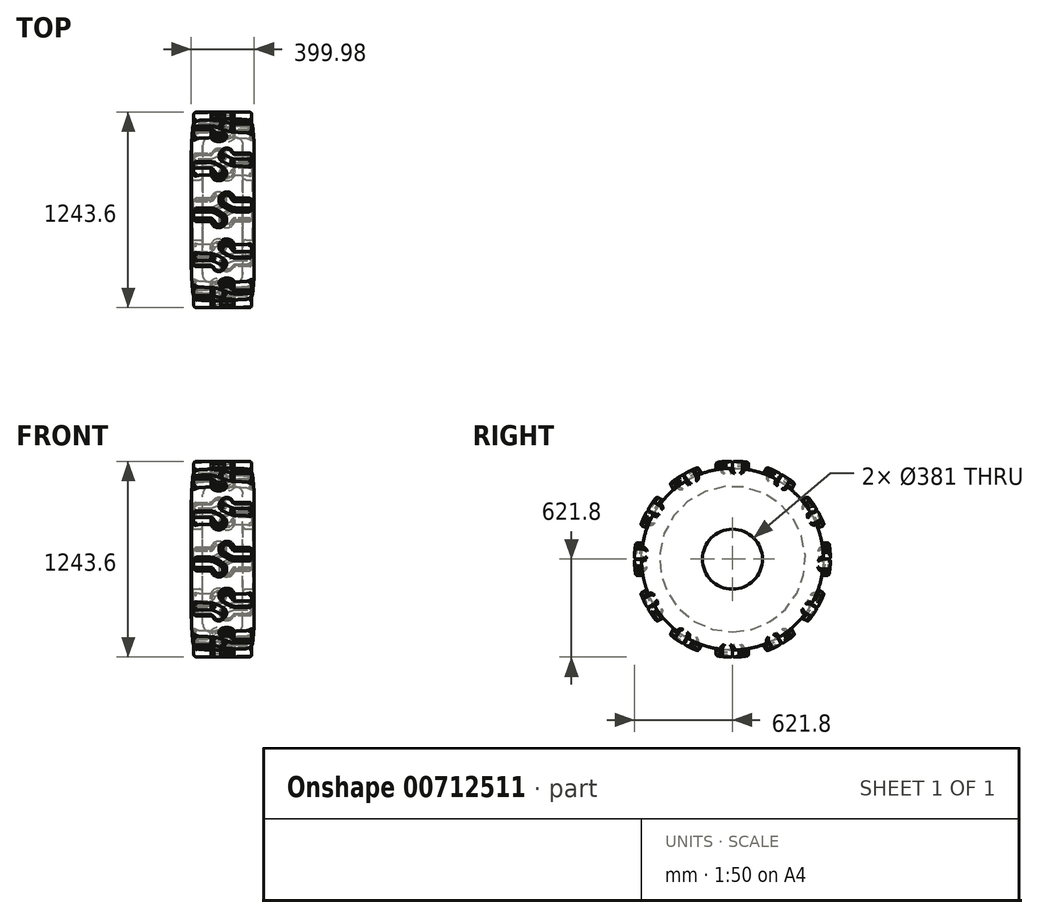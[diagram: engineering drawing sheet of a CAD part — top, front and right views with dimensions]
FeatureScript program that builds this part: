
annotation { "Feature Type Name" : "Feature", "Feature Type Description" : "" }
export const myFeature = defineFeature(function(context is Context, id is Id, definition is map)
    precondition{}
    {
        {
            var Q0;
            Q0=qCreatedBy(makeId("Front.planeOp"),FACE);
            var sketch = newSketch(context, id + "F0", { "sketchPlane" : qUnion([Q0])});
            skLineSegment(sketch, "E0", {"start": v(-266.7, 0) * mm, "end": v(266.7, 0) * mm, "construction": true});
            skLineSegment(sketch, "E1", {"start": v(-190.5, 571.5) * mm, "end": v(190.5, 571.5) * mm, "construction": true});
            skLineSegment(sketch, "E2", {"start": v(0, 0) * mm, "end": v(0, 647.7) * mm, "construction": true});
            skArc(sketch, "E3.trimOffspring", {"start": v(142.07, 574.15) * mm, "mid": v(0, 577.46) * mm, "end": v(-142.07, 574.15) * mm});
            skPoint(sketch, "E4", {"position": v(0, 571.5) * mm});
            skPoint(sketch, "E5.visualSharp", {"position": v(-190.5, 571.5) * mm});
            skArc(sketch, "E5.filletArc", {"start": v(-142.07, 574.15) * mm, "mid": v(-175.89, 559.06) * mm, "end": v(-190.47, 525.02) * mm});
            skPoint(sketch, "E6.visualSharp", {"position": v(190.5, 571.5) * mm});
            skArc(sketch, "E6.filletArc", {"start": v(190.47, 525.02) * mm, "mid": v(175.89, 559.06) * mm, "end": v(142.07, 574.15) * mm});
            skLineSegment(sketch, "E7", {"start": v(-190.5, 0) * mm, "end": v(190.5, 0) * mm});
            skArc(sketch, "E8", {"start": v(-190.74, 521.16) * mm, "mid": v(-194.18, 485.58) * mm, "end": v(-196.78, 449.92) * mm});
            skArc(sketch, "E9", {"start": v(190.5, 190.5) * mm, "mid": v(197.8, 282.59) * mm, "end": v(199.51, 374.95) * mm});
            skLineSegment(sketch, "E10", {"start": v(-190.5, 190.5) * mm, "end": v(190.5, 190.5) * mm});
            skLineSegment(sketch, "E11", {"start": v(-190.5, 190.5) * mm, "end": v(-190.5, 0) * mm});
            skLineSegment(sketch, "E12", {"start": v(190.5, 190.5) * mm, "end": v(190.5, 0) * mm});
            skPoint(sketch, "E13.visualSharp", {"position": v(-190.5, 523.4) * mm});
            skArc(sketch, "E13.filletArc", {"start": v(-190.74, 521.16) * mm, "mid": v(-190.57, 523.09) * mm, "end": v(-190.47, 525.02) * mm});
            skPoint(sketch, "E14.visualSharp", {"position": v(190.5, 523.4) * mm});
            skArc(sketch, "E14.filletArc", {"start": v(190.47, 525.02) * mm, "mid": v(190.57, 523.09) * mm, "end": v(190.74, 521.16) * mm});
            skLineSegment(sketch, "E15", {"start": v(190.5, 0) * mm, "end": v(190.5, 571.5) * mm, "construction": true});
            skLineSegment(sketch, "E16", {"start": v(-190.5, 571.5) * mm, "end": v(-190.5, 0) * mm, "construction": true});
            skArc(sketch, "E17", {"start": v(-197.04, 448.94) * mm, "mid": v(-197.44, 447.47) * mm, "end": v(-197.22, 445.96) * mm});
            skArc(sketch, "E18", {"start": v(-199.66, 378.93) * mm, "mid": v(-199.99, 377.44) * mm, "end": v(-199.7, 375.94) * mm});
            skArc(sketch, "E19.trimOffspring", {"start": v(-199.51, 374.95) * mm, "mid": v(-197.8, 282.59) * mm, "end": v(-190.5, 190.5) * mm});
            skArc(sketch, "E20.trimOffspring", {"start": v(-197.07, 444.95) * mm, "mid": v(-198.6, 412.45) * mm, "end": v(-199.44, 379.92) * mm});
            skPoint(sketch, "E21.visualSharp", {"position": v(-197.04, 445.54) * mm});
            skArc(sketch, "E21.filletArc", {"start": v(-197.07, 444.95) * mm, "mid": v(-197.1, 445.46) * mm, "end": v(-197.22, 445.96) * mm});
            skPoint(sketch, "E22.visualSharp", {"position": v(-196.81, 449.34) * mm});
            skArc(sketch, "E22.filletArc", {"start": v(-197.04, 448.94) * mm, "mid": v(-196.86, 449.42) * mm, "end": v(-196.78, 449.92) * mm});
            skPoint(sketch, "E23.visualSharp", {"position": v(-199.45, 379.34) * mm});
            skArc(sketch, "E23.filletArc", {"start": v(-199.66, 378.93) * mm, "mid": v(-199.5, 379.42) * mm, "end": v(-199.44, 379.92) * mm});
            skPoint(sketch, "E24.visualSharp", {"position": v(-199.5, 375.53) * mm});
            skArc(sketch, "E24.filletArc", {"start": v(-199.51, 374.95) * mm, "mid": v(-199.56, 375.45) * mm, "end": v(-199.7, 375.94) * mm});
            skArc(sketch, "E25.MirrorCS", {"start": v(197.04, 448.94) * mm, "mid": v(197.44, 447.47) * mm, "end": v(197.22, 445.96) * mm});
            skArc(sketch, "E26.MirrorCS", {"start": v(197.04, 448.94) * mm, "mid": v(196.86, 449.42) * mm, "end": v(196.78, 449.92) * mm});
            skArc(sketch, "E27.MirrorCS", {"start": v(197.07, 444.95) * mm, "mid": v(197.1, 445.46) * mm, "end": v(197.22, 445.96) * mm});
            skArc(sketch, "E28.MirrorCS", {"start": v(199.66, 378.93) * mm, "mid": v(199.99, 377.44) * mm, "end": v(199.7, 375.94) * mm});
            skArc(sketch, "E29.MirrorCS", {"start": v(199.66, 378.93) * mm, "mid": v(199.5, 379.42) * mm, "end": v(199.44, 379.92) * mm});
            skArc(sketch, "E30.MirrorCS", {"start": v(199.51, 374.95) * mm, "mid": v(199.56, 375.45) * mm, "end": v(199.7, 375.94) * mm});
            skArc(sketch, "E31.trimOffspring", {"start": v(196.78, 449.92) * mm, "mid": v(194.18, 485.58) * mm, "end": v(190.74, 521.16) * mm});
            skArc(sketch, "E32.trimOffspring", {"start": v(199.44, 379.92) * mm, "mid": v(198.6, 412.45) * mm, "end": v(197.07, 444.95) * mm});
            skSolve(sketch);
        }
        {
            var Q0;
            Q0 = qSketchRegion(id + "F0", true);
            var Q1;
            Q1=sQuery(id+"F0.wireOp",EDGE,"E0");
            revolve(context, id + "F1", {"surfaceOperationType" : NewSurfaceOperationType.NEW, "entities" : qUnion([Q0]), "axis" : qUnion([Q1]), "revolveType" : RevolveType.FULL});
        }
        {
            var Q0;
            Q0=qCreatedBy(makeId("Top.planeOp"),FACE);
            var sketch = newSketch(context, id + "F2", { "sketchPlane" : qUnion([Q0])});
            skLineSegment(sketch, "E33", {"start": v(-184.12, -12.7) * mm, "end": v(-184.12, -50.8) * mm});
            skLineSegment(sketch, "E34", {"start": v(-171.42, -63.5) * mm, "end": v(-82.52, -63.5) * mm});
            skLineSegment(sketch, "E35", {"start": v(-88.6, -52.13) * mm, "end": v(-57.12, -70.3) * mm});
            skLineSegment(sketch, "E36", {"start": v(-6.35, -32.2) * mm, "end": v(-44.42, -10.2) * mm});
            skLineSegment(sketch, "E37", {"start": v(-82.52, 0) * mm, "end": v(-171.42, 0) * mm});
            skLineSegment(sketch, "E38", {"start": v(0, 708.1) * mm, "end": v(0, -708.1) * mm, "construction": true});
            skArc(sketch, "E39", {"start": v(-59.17, -82.83) * mm, "mid": v(0.97, -92.69) * mm, "end": v(-6.35, -32.2) * mm});
            skPoint(sketch, "E40.visualSharp", {"position": v(-62.1, 0) * mm});
            skArc(sketch, "E40.filletArc", {"start": v(-44.42, -10.2) * mm, "mid": v(-62.8, -2.6) * mm, "end": v(-82.52, 0) * mm});
            skArc(sketch, "E41.filletArc", {"start": v(-57.12, -70.3) * mm, "mid": v(-69.38, -65.23) * mm, "end": v(-82.52, -63.5) * mm});
            skPoint(sketch, "E42.visualSharp", {"position": v(-63.47, -66.64) * mm});
            skArc(sketch, "E42.filletArc", {"start": v(-59.17, -82.83) * mm, "mid": v(-71.7, -65.39) * mm, "end": v(-88.6, -52.13) * mm});
            skPoint(sketch, "E43.visualSharp", {"position": v(-184.12, 0) * mm});
            skArc(sketch, "E43.filletArc", {"start": v(-171.42, 0) * mm, "mid": v(-180.4, -3.72) * mm, "end": v(-184.12, -12.7) * mm});
            skPoint(sketch, "E44.visualSharp", {"position": v(-184.12, -63.5) * mm});
            skArc(sketch, "E44.filletArc", {"start": v(-184.12, -50.8) * mm, "mid": v(-180.4, -59.78) * mm, "end": v(-171.42, -63.5) * mm});
            skPoint(sketch, "E45.MirrorP", {"position": v(63.47, -66.64) * mm});
            skLineSegment(sketch, "E46", {"start": v(-306.91, 0) * mm, "end": v(266.7, 0) * mm, "construction": true});
            skSolve(sketch);
        }
        {
            var Q0;
            Q0 = qSketchRegion(id + "F2", true);
            var Q1;
            Q1=sQuery(id+"F0.wireOp",VERTEX,"E2.end");
            extrude(context, id + "F3", {"entities" : qUnion([Q0]), "endBound" : BoundingType.UP_TO_VERTEX, "depth" : 711.2 * mm, "endBoundEntityVertex" : qUnion([Q1]), "offsetDistance" : 25.4 * mm});
        }
        {
            var Q0;
            Q0=makeQuery(id+"F3.opExtrude","SWEPT_BODY",BODY,{"disambiguationData":[OSD([sQuery(id+"F2.wireOp",EDGE,"E33"),sQuery(id+"F2.wireOp",EDGE,"E34"),sQuery(id+"F2.wireOp",EDGE,"E35"),sQuery(id+"F2.wireOp",EDGE,"E36"),sQuery(id+"F2.wireOp",EDGE,"E37"),sQuery(id+"F2.wireOp",EDGE,"E39"),sQuery(id+"F2.wireOp",EDGE,"E40.filletArc"),sQuery(id+"F2.wireOp",EDGE,"E41.filletArc"),sQuery(id+"F2.wireOp",EDGE,"E42.filletArc"),sQuery(id+"F2.wireOp",EDGE,"E43.filletArc"),sQuery(id+"F2.wireOp",EDGE,"E44.filletArc")])]});
            var Q1;
            Q1=qCreatedBy(makeId("Right.planeOp"),FACE);
            mirror(context, id + "F4", {"entities" : qUnion([Q0]), "mirrorPlane" : qUnion([Q1])});
        }
        {
            var Q0;
            Q0=makeQuery(id+"F4.opPattern","COPY",BODY,{"derivedFrom":makeQuery(id+"F3.opExtrude","SWEPT_BODY",BODY,{"disambiguationData":[OSD([sQuery(id+"F2.wireOp",EDGE,"E33"),sQuery(id+"F2.wireOp",EDGE,"E34"),sQuery(id+"F2.wireOp",EDGE,"E35"),sQuery(id+"F2.wireOp",EDGE,"E36"),sQuery(id+"F2.wireOp",EDGE,"E37"),sQuery(id+"F2.wireOp",EDGE,"E39"),sQuery(id+"F2.wireOp",EDGE,"E40.filletArc"),sQuery(id+"F2.wireOp",EDGE,"E41.filletArc"),sQuery(id+"F2.wireOp",EDGE,"E42.filletArc"),sQuery(id+"F2.wireOp",EDGE,"E43.filletArc"),sQuery(id+"F2.wireOp",EDGE,"E44.filletArc")])]}),"instanceName":"1"});
            var Q1;
            Q1=qCreatedBy(makeId("Front.planeOp"),FACE);
            mirror(context, id + "F5", {"entities" : qUnion([Q0]), "mirrorPlane" : qUnion([Q1])});
        }
        {
            var Q0;
            Q0=makeQuery(id+"F4.opPattern","COPY",BODY,{"derivedFrom":makeQuery(id+"F3.opExtrude","SWEPT_BODY",BODY,{"disambiguationData":[OSD([sQuery(id+"F2.wireOp",EDGE,"E33"),sQuery(id+"F2.wireOp",EDGE,"E34"),sQuery(id+"F2.wireOp",EDGE,"E35"),sQuery(id+"F2.wireOp",EDGE,"E36"),sQuery(id+"F2.wireOp",EDGE,"E37"),sQuery(id+"F2.wireOp",EDGE,"E39"),sQuery(id+"F2.wireOp",EDGE,"E40.filletArc"),sQuery(id+"F2.wireOp",EDGE,"E41.filletArc"),sQuery(id+"F2.wireOp",EDGE,"E42.filletArc"),sQuery(id+"F2.wireOp",EDGE,"E43.filletArc"),sQuery(id+"F2.wireOp",EDGE,"E44.filletArc")])]}),"instanceName":"1"});
            deleteBodies(context, id + "F6", {"entities" : qUnion([Q0])});
        }
        {
            var Q0;
            Q0=qCreatedBy(makeId("Front.planeOp"),FACE);
            var sketch = newSketch(context, id + "F7", { "sketchPlane" : qUnion([Q0])});
            skLineSegment(sketch, "E47", {"start": v(-266.7, 0) * mm, "end": v(266.7, 0) * mm, "construction": true});
            skArc(sketch, "E48", {"start": v(266.7, 616.91) * mm, "mid": v(0, 622.3) * mm, "end": v(-266.7, 616.91) * mm});
            skLineSegment(sketch, "E49", {"start": v(266.7, 616.91) * mm, "end": v(266.7, 673.1) * mm});
            skLineSegment(sketch, "E50", {"start": v(266.7, 622.3) * mm, "end": v(-266.7, 622.3) * mm, "construction": true});
            skLineSegment(sketch, "E51", {"start": v(-266.7, 673.1) * mm, "end": v(-266.7, 616.91) * mm});
            skLineSegment(sketch, "E52", {"start": v(0, 0) * mm, "end": v(0, 635) * mm, "construction": true});
            skLineSegment(sketch, "E53", {"start": v(-266.7, 673.1) * mm, "end": v(266.7, 673.1) * mm});
            skSolve(sketch);
        }
        {
            var Q0;
            Q0 = qSketchRegion(id + "F7", true);
            var Q1;
            Q1=sQuery(id+"F7.wireOp",EDGE,"E47");
            revolve(context, id + "F8", {"operationType" : NewBodyOperationType.REMOVE, "surfaceOperationType" : NewSurfaceOperationType.NEW, "entities" : qUnion([Q0]), "axis" : qUnion([Q1]), "revolveType" : RevolveType.FULL, "oppositeDirection" : true});
        }
        {
            var Q0;
            Q0=makeQuery(id+"F3.opExtrude","SWEPT_BODY",BODY,{"disambiguationData":[OSD([sQuery(id+"F2.wireOp",EDGE,"E33"),sQuery(id+"F2.wireOp",EDGE,"E34"),sQuery(id+"F2.wireOp",EDGE,"E35"),sQuery(id+"F2.wireOp",EDGE,"E36"),sQuery(id+"F2.wireOp",EDGE,"E37"),sQuery(id+"F2.wireOp",EDGE,"E39"),sQuery(id+"F2.wireOp",EDGE,"E40.filletArc"),sQuery(id+"F2.wireOp",EDGE,"E41.filletArc"),sQuery(id+"F2.wireOp",EDGE,"E42.filletArc"),sQuery(id+"F2.wireOp",EDGE,"E43.filletArc"),sQuery(id+"F2.wireOp",EDGE,"E44.filletArc")])]});
            var Q1;
            Q1=makeQuery(id+"F5.opPattern","COPY",BODY,{"derivedFrom":makeQuery(id+"F4.opPattern","COPY",BODY,{"derivedFrom":makeQuery(id+"F3.opExtrude","SWEPT_BODY",BODY,{"disambiguationData":[OSD([sQuery(id+"F2.wireOp",EDGE,"E33"),sQuery(id+"F2.wireOp",EDGE,"E34"),sQuery(id+"F2.wireOp",EDGE,"E35"),sQuery(id+"F2.wireOp",EDGE,"E36"),sQuery(id+"F2.wireOp",EDGE,"E37"),sQuery(id+"F2.wireOp",EDGE,"E39"),sQuery(id+"F2.wireOp",EDGE,"E40.filletArc"),sQuery(id+"F2.wireOp",EDGE,"E41.filletArc"),sQuery(id+"F2.wireOp",EDGE,"E42.filletArc"),sQuery(id+"F2.wireOp",EDGE,"E43.filletArc"),sQuery(id+"F2.wireOp",EDGE,"E44.filletArc")])]}),"instanceName":"1"}),"instanceName":"1"});
            var Q2;
            Q2=makeQuery(id+"F1.opRevolve","SWEPT_EDGE",EDGE,{"disambiguationData":[OSD([sQuery(id+"F0.wireOp",EDGE,"E3.trimOffspring"),sQuery(id+"F0.wireOp",EDGE,"E5.filletArc")])]});
            circularPattern(context, id + "F9", {"operationType" : NewBodyOperationType.ADD, "entities" : qUnion([Q0, Q1]), "axis" : qUnion([Q2]), "angle" : 360 * degree, "instanceCount" : 12, "equalSpace" : true, "isCentered" : true});
        }
        {
            var Q0;
            Q0=makeQuery(id+"F8.boolean.opBoolean","INTERSECT",EDGE,{"derivedFrom":[makeQuery(id+"F3.opExtrude","SWEPT_FACE",FACE,{"disambiguationData":[OSD([sQuery(id+"F2.wireOp",EDGE,"E35")])]}),makeQuery(id+"F8.opRevolve","SWEPT_FACE",FACE,{"disambiguationData":[OSD([sQuery(id+"F7.wireOp",EDGE,"E48")])]})]});
            var Q1;
            {var subQ0=makeQuery(id+"F3.opExtrude","SWEPT_FACE",FACE,{"disambiguationData":[OSD([sQuery(id+"F2.wireOp",EDGE,"E33")])]});Q1=makeQuery(id+"F9.boolean.opBoolean","INTERSECT",EDGE,{"disambiguationData":[OD(0.0)],"derivedFrom":[makeQuery(id+"F1.opRevolve","SWEPT_FACE",FACE,{"disambiguationData":[OSD([sQuery(id+"F0.wireOp",EDGE,"E5.filletArc")])]}),subQ0,makeQuery(id+"F9.opPattern","COPY",FACE,{"derivedFrom":subQ0,"instanceName":"-11"}),makeQuery(id+"F9.opPattern","COPY",FACE,{"derivedFrom":subQ0,"instanceName":"-10"}),makeQuery(id+"F9.opPattern","COPY",FACE,{"derivedFrom":subQ0,"instanceName":"-9"}),makeQuery(id+"F9.opPattern","COPY",FACE,{"derivedFrom":subQ0,"instanceName":"-8"}),makeQuery(id+"F9.opPattern","COPY",FACE,{"derivedFrom":subQ0,"instanceName":"-7"}),makeQuery(id+"F9.opPattern","COPY",FACE,{"derivedFrom":subQ0,"instanceName":"-6"}),makeQuery(id+"F9.opPattern","COPY",FACE,{"derivedFrom":subQ0,"instanceName":"-5"}),makeQuery(id+"F9.opPattern","COPY",FACE,{"derivedFrom":subQ0,"instanceName":"-4"}),makeQuery(id+"F9.opPattern","COPY",FACE,{"derivedFrom":subQ0,"instanceName":"-3"}),makeQuery(id+"F9.opPattern","COPY",FACE,{"derivedFrom":subQ0,"instanceName":"-2"}),makeQuery(id+"F9.opPattern","COPY",FACE,{"derivedFrom":subQ0,"instanceName":"-1"}),makeQuery(id+"F9.opPattern","COPY",FACE,{"derivedFrom":subQ0,"instanceName":"1"}),makeQuery(id+"F9.opPattern","COPY",FACE,{"derivedFrom":subQ0,"instanceName":"2"}),makeQuery(id+"F9.opPattern","COPY",FACE,{"derivedFrom":subQ0,"instanceName":"3"}),makeQuery(id+"F9.opPattern","COPY",FACE,{"derivedFrom":subQ0,"instanceName":"4"}),makeQuery(id+"F9.opPattern","COPY",FACE,{"derivedFrom":subQ0,"instanceName":"5"}),makeQuery(id+"F9.opPattern","COPY",FACE,{"derivedFrom":subQ0,"instanceName":"6"}),makeQuery(id+"F9.opPattern","COPY",FACE,{"derivedFrom":subQ0,"instanceName":"7"}),makeQuery(id+"F9.opPattern","COPY",FACE,{"derivedFrom":subQ0,"instanceName":"8"}),makeQuery(id+"F9.opPattern","COPY",FACE,{"derivedFrom":subQ0,"instanceName":"9"}),makeQuery(id+"F9.opPattern","COPY",FACE,{"derivedFrom":subQ0,"instanceName":"10"}),makeQuery(id+"F9.opPattern","COPY",FACE,{"derivedFrom":subQ0,"instanceName":"11"})]});}
            var Q2;
            Q2=makeQuery(id+"F9.boolean.opBoolean","INTERSECT",EDGE,{"derivedFrom":[makeQuery(id+"F1.opRevolve","SWEPT_FACE",FACE,{"disambiguationData":[OSD([sQuery(id+"F0.wireOp",EDGE,"E3.trimOffspring")])]}),makeQuery(id+"F5.opPattern","COPY",FACE,{"derivedFrom":makeQuery(id+"F4.opPattern","COPY",FACE,{"derivedFrom":makeQuery(id+"F3.opExtrude","SWEPT_FACE",FACE,{"disambiguationData":[OSD([sQuery(id+"F2.wireOp",EDGE,"E36")])]}),"instanceName":"1"}),"instanceName":"1"})]});
            var Q3;
            Q3=makeQuery(id+"F8.boolean.opBoolean","INTERSECT",EDGE,{"derivedFrom":[makeQuery(id+"F5.opPattern","COPY",FACE,{"derivedFrom":makeQuery(id+"F4.opPattern","COPY",FACE,{"derivedFrom":makeQuery(id+"F3.opExtrude","SWEPT_FACE",FACE,{"disambiguationData":[OSD([sQuery(id+"F2.wireOp",EDGE,"E36")])]}),"instanceName":"1"}),"instanceName":"1"}),makeQuery(id+"F8.opRevolve","SWEPT_FACE",FACE,{"disambiguationData":[OSD([sQuery(id+"F7.wireOp",EDGE,"E48")])]})]});
            var Q4;
            Q4=makeQuery(id+"F9.opPattern","COPY",EDGE,{"derivedFrom":makeQuery(id+"F8.boolean.opBoolean","INTERSECT",EDGE,{"derivedFrom":[makeQuery(id+"F5.opPattern","COPY",FACE,{"derivedFrom":makeQuery(id+"F4.opPattern","COPY",FACE,{"derivedFrom":makeQuery(id+"F3.opExtrude","SWEPT_FACE",FACE,{"disambiguationData":[OSD([sQuery(id+"F2.wireOp",EDGE,"E39")])]}),"instanceName":"1"}),"instanceName":"1"}),makeQuery(id+"F8.opRevolve","SWEPT_FACE",FACE,{"disambiguationData":[OSD([sQuery(id+"F7.wireOp",EDGE,"E48")])]})]}),"instanceName":"-1"});
            var Q5;
            Q5=makeQuery(id+"F9.boolean.opBoolean","INTERSECT",EDGE,{"derivedFrom":[makeQuery(id+"F1.opRevolve","SWEPT_FACE",FACE,{"disambiguationData":[OSD([sQuery(id+"F0.wireOp",EDGE,"E3.trimOffspring")])]}),makeQuery(id+"F9.opPattern","COPY",FACE,{"derivedFrom":makeQuery(id+"F5.opPattern","COPY",FACE,{"derivedFrom":makeQuery(id+"F4.opPattern","COPY",FACE,{"derivedFrom":makeQuery(id+"F3.opExtrude","SWEPT_FACE",FACE,{"disambiguationData":[OSD([sQuery(id+"F2.wireOp",EDGE,"E39")])]}),"instanceName":"1"}),"instanceName":"1"}),"instanceName":"-1"})]});
            var Q6;
            Q6=makeQuery(id+"F9.opPattern","COPY",EDGE,{"derivedFrom":makeQuery(id+"F8.boolean.opBoolean","INTERSECT",EDGE,{"derivedFrom":[makeQuery(id+"F3.opExtrude","SWEPT_FACE",FACE,{"disambiguationData":[OSD([sQuery(id+"F2.wireOp",EDGE,"E37")])]}),makeQuery(id+"F8.opRevolve","SWEPT_FACE",FACE,{"disambiguationData":[OSD([sQuery(id+"F7.wireOp",EDGE,"E48")])]})]}),"instanceName":"-1"});
            var Q7;
            Q7=makeQuery(id+"F9.boolean.opBoolean","INTERSECT",EDGE,{"derivedFrom":[makeQuery(id+"F1.opRevolve","SWEPT_FACE",FACE,{"disambiguationData":[OSD([sQuery(id+"F0.wireOp",EDGE,"E3.trimOffspring")])]}),makeQuery(id+"F9.opPattern","COPY",FACE,{"derivedFrom":makeQuery(id+"F3.opExtrude","SWEPT_FACE",FACE,{"disambiguationData":[OSD([sQuery(id+"F2.wireOp",EDGE,"E37")])]}),"instanceName":"-1"})]});
            var Q8;
            Q8=makeQuery(id+"F9.opPattern","COPY",EDGE,{"derivedFrom":makeQuery(id+"F8.boolean.opBoolean","INTERSECT",EDGE,{"derivedFrom":[makeQuery(id+"F3.opExtrude","SWEPT_FACE",FACE,{"disambiguationData":[OSD([sQuery(id+"F2.wireOp",EDGE,"E39")])]}),makeQuery(id+"F8.opRevolve","SWEPT_FACE",FACE,{"disambiguationData":[OSD([sQuery(id+"F7.wireOp",EDGE,"E48")])]})]}),"instanceName":"-2"});
            var Q9;
            Q9=makeQuery(id+"F9.opPattern","COPY",EDGE,{"derivedFrom":makeQuery(id+"F8.boolean.opBoolean","INTERSECT",EDGE,{"derivedFrom":[makeQuery(id+"F5.opPattern","COPY",FACE,{"derivedFrom":makeQuery(id+"F4.opPattern","COPY",FACE,{"derivedFrom":makeQuery(id+"F3.opExtrude","SWEPT_FACE",FACE,{"disambiguationData":[OSD([sQuery(id+"F2.wireOp",EDGE,"E36")])]}),"instanceName":"1"}),"instanceName":"1"}),makeQuery(id+"F8.opRevolve","SWEPT_FACE",FACE,{"disambiguationData":[OSD([sQuery(id+"F7.wireOp",EDGE,"E48")])]})]}),"instanceName":"-2"});
            var Q10;
            Q10=makeQuery(id+"F9.boolean.opBoolean","INTERSECT",EDGE,{"derivedFrom":[makeQuery(id+"F1.opRevolve","SWEPT_FACE",FACE,{"disambiguationData":[OSD([sQuery(id+"F0.wireOp",EDGE,"E3.trimOffspring")])]}),makeQuery(id+"F9.opPattern","COPY",FACE,{"derivedFrom":makeQuery(id+"F5.opPattern","COPY",FACE,{"derivedFrom":makeQuery(id+"F4.opPattern","COPY",FACE,{"derivedFrom":makeQuery(id+"F3.opExtrude","SWEPT_FACE",FACE,{"disambiguationData":[OSD([sQuery(id+"F2.wireOp",EDGE,"E36")])]}),"instanceName":"1"}),"instanceName":"1"}),"instanceName":"-2"})]});
            var Q11;
            Q11=makeQuery(id+"F9.boolean.opBoolean","INTERSECT",EDGE,{"derivedFrom":[makeQuery(id+"F1.opRevolve","SWEPT_FACE",FACE,{"disambiguationData":[OSD([sQuery(id+"F0.wireOp",EDGE,"E3.trimOffspring")])]}),makeQuery(id+"F9.opPattern","COPY",FACE,{"derivedFrom":makeQuery(id+"F3.opExtrude","SWEPT_FACE",FACE,{"disambiguationData":[OSD([sQuery(id+"F2.wireOp",EDGE,"E39")])]}),"instanceName":"-2"})]});
            var Q12;
            Q12=makeQuery(id+"F9.opPattern","COPY",EDGE,{"derivedFrom":makeQuery(id+"F8.boolean.opBoolean","INTERSECT",EDGE,{"derivedFrom":[makeQuery(id+"F3.opExtrude","SWEPT_FACE",FACE,{"disambiguationData":[OSD([sQuery(id+"F2.wireOp",EDGE,"E39")])]}),makeQuery(id+"F8.opRevolve","SWEPT_FACE",FACE,{"disambiguationData":[OSD([sQuery(id+"F7.wireOp",EDGE,"E48")])]})]}),"instanceName":"-3"});
            var Q13;
            Q13=makeQuery(id+"F9.opPattern","COPY",EDGE,{"derivedFrom":makeQuery(id+"F8.boolean.opBoolean","INTERSECT",EDGE,{"derivedFrom":[makeQuery(id+"F5.opPattern","COPY",FACE,{"derivedFrom":makeQuery(id+"F4.opPattern","COPY",FACE,{"derivedFrom":makeQuery(id+"F3.opExtrude","SWEPT_FACE",FACE,{"disambiguationData":[OSD([sQuery(id+"F2.wireOp",EDGE,"E36")])]}),"instanceName":"1"}),"instanceName":"1"}),makeQuery(id+"F8.opRevolve","SWEPT_FACE",FACE,{"disambiguationData":[OSD([sQuery(id+"F7.wireOp",EDGE,"E48")])]})]}),"instanceName":"-4"});
            var Q14;
            Q14=makeQuery(id+"F9.boolean.opBoolean","INTERSECT",EDGE,{"derivedFrom":[makeQuery(id+"F1.opRevolve","SWEPT_FACE",FACE,{"disambiguationData":[OSD([sQuery(id+"F0.wireOp",EDGE,"E3.trimOffspring")])]}),makeQuery(id+"F9.opPattern","COPY",FACE,{"derivedFrom":makeQuery(id+"F3.opExtrude","SWEPT_FACE",FACE,{"disambiguationData":[OSD([sQuery(id+"F2.wireOp",EDGE,"E39")])]}),"instanceName":"-3"})]});
            var Q15;
            Q15=makeQuery(id+"F9.boolean.opBoolean","INTERSECT",EDGE,{"derivedFrom":[makeQuery(id+"F1.opRevolve","SWEPT_FACE",FACE,{"disambiguationData":[OSD([sQuery(id+"F0.wireOp",EDGE,"E3.trimOffspring")])]}),makeQuery(id+"F9.opPattern","COPY",FACE,{"derivedFrom":makeQuery(id+"F5.opPattern","COPY",FACE,{"derivedFrom":makeQuery(id+"F4.opPattern","COPY",FACE,{"derivedFrom":makeQuery(id+"F3.opExtrude","SWEPT_FACE",FACE,{"disambiguationData":[OSD([sQuery(id+"F2.wireOp",EDGE,"E40.filletArc")])]}),"instanceName":"1"}),"instanceName":"1"}),"instanceName":"-4"})]});
            var Q16;
            Q16=makeQuery(id+"F9.opPattern","COPY",EDGE,{"derivedFrom":makeQuery(id+"F8.boolean.opBoolean","INTERSECT",EDGE,{"derivedFrom":[makeQuery(id+"F3.opExtrude","SWEPT_FACE",FACE,{"disambiguationData":[OSD([sQuery(id+"F2.wireOp",EDGE,"E39")])]}),makeQuery(id+"F8.opRevolve","SWEPT_FACE",FACE,{"disambiguationData":[OSD([sQuery(id+"F7.wireOp",EDGE,"E48")])]})]}),"instanceName":"-4"});
            var Q17;
            Q17=makeQuery(id+"F9.boolean.opBoolean","INTERSECT",EDGE,{"derivedFrom":[makeQuery(id+"F1.opRevolve","SWEPT_FACE",FACE,{"disambiguationData":[OSD([sQuery(id+"F0.wireOp",EDGE,"E3.trimOffspring")])]}),makeQuery(id+"F9.opPattern","COPY",FACE,{"derivedFrom":makeQuery(id+"F3.opExtrude","SWEPT_FACE",FACE,{"disambiguationData":[OSD([sQuery(id+"F2.wireOp",EDGE,"E39")])]}),"instanceName":"-4"})]});
            var Q18;
            Q18=makeQuery(id+"F9.opPattern","COPY",EDGE,{"derivedFrom":makeQuery(id+"F8.boolean.opBoolean","INTERSECT",EDGE,{"derivedFrom":[makeQuery(id+"F3.opExtrude","SWEPT_FACE",FACE,{"disambiguationData":[OSD([sQuery(id+"F2.wireOp",EDGE,"E39")])]}),makeQuery(id+"F8.opRevolve","SWEPT_FACE",FACE,{"disambiguationData":[OSD([sQuery(id+"F7.wireOp",EDGE,"E48")])]})]}),"instanceName":"-8"});
            var Q19;
            Q19=makeQuery(id+"F9.boolean.opBoolean","INTERSECT",EDGE,{"derivedFrom":[makeQuery(id+"F1.opRevolve","SWEPT_FACE",FACE,{"disambiguationData":[OSD([sQuery(id+"F0.wireOp",EDGE,"E3.trimOffspring")])]}),makeQuery(id+"F9.opPattern","COPY",FACE,{"derivedFrom":makeQuery(id+"F3.opExtrude","SWEPT_FACE",FACE,{"disambiguationData":[OSD([sQuery(id+"F2.wireOp",EDGE,"E39")])]}),"instanceName":"-8"})]});
            var Q20;
            Q20=makeQuery(id+"F9.opPattern","COPY",EDGE,{"derivedFrom":makeQuery(id+"F8.boolean.opBoolean","INTERSECT",EDGE,{"derivedFrom":[makeQuery(id+"F5.opPattern","COPY",FACE,{"derivedFrom":makeQuery(id+"F4.opPattern","COPY",FACE,{"derivedFrom":makeQuery(id+"F3.opExtrude","SWEPT_FACE",FACE,{"disambiguationData":[OSD([sQuery(id+"F2.wireOp",EDGE,"E36")])]}),"instanceName":"1"}),"instanceName":"1"}),makeQuery(id+"F8.opRevolve","SWEPT_FACE",FACE,{"disambiguationData":[OSD([sQuery(id+"F7.wireOp",EDGE,"E48")])]})]}),"instanceName":"-8"});
            var Q21;
            Q21=makeQuery(id+"F9.boolean.opBoolean","INTERSECT",EDGE,{"derivedFrom":[makeQuery(id+"F1.opRevolve","SWEPT_FACE",FACE,{"disambiguationData":[OSD([sQuery(id+"F0.wireOp",EDGE,"E3.trimOffspring")])]}),makeQuery(id+"F9.opPattern","COPY",FACE,{"derivedFrom":makeQuery(id+"F5.opPattern","COPY",FACE,{"derivedFrom":makeQuery(id+"F4.opPattern","COPY",FACE,{"derivedFrom":makeQuery(id+"F3.opExtrude","SWEPT_FACE",FACE,{"disambiguationData":[OSD([sQuery(id+"F2.wireOp",EDGE,"E36")])]}),"instanceName":"1"}),"instanceName":"1"}),"instanceName":"-8"})]});
            var Q22;
            Q22=makeQuery(id+"F9.opPattern","COPY",EDGE,{"derivedFrom":makeQuery(id+"F8.boolean.opBoolean","INTERSECT",EDGE,{"derivedFrom":[makeQuery(id+"F5.opPattern","COPY",FACE,{"derivedFrom":makeQuery(id+"F4.opPattern","COPY",FACE,{"derivedFrom":makeQuery(id+"F3.opExtrude","SWEPT_FACE",FACE,{"disambiguationData":[OSD([sQuery(id+"F2.wireOp",EDGE,"E39")])]}),"instanceName":"1"}),"instanceName":"1"}),makeQuery(id+"F8.opRevolve","SWEPT_FACE",FACE,{"disambiguationData":[OSD([sQuery(id+"F7.wireOp",EDGE,"E48")])]})]}),"instanceName":"-9"});
            var Q23;
            Q23=makeQuery(id+"F9.boolean.opBoolean","INTERSECT",EDGE,{"derivedFrom":[makeQuery(id+"F1.opRevolve","SWEPT_FACE",FACE,{"disambiguationData":[OSD([sQuery(id+"F0.wireOp",EDGE,"E3.trimOffspring")])]}),makeQuery(id+"F9.opPattern","COPY",FACE,{"derivedFrom":makeQuery(id+"F5.opPattern","COPY",FACE,{"derivedFrom":makeQuery(id+"F4.opPattern","COPY",FACE,{"derivedFrom":makeQuery(id+"F3.opExtrude","SWEPT_FACE",FACE,{"disambiguationData":[OSD([sQuery(id+"F2.wireOp",EDGE,"E36")])]}),"instanceName":"1"}),"instanceName":"1"}),"instanceName":"-9"})]});
            var Q24;
            Q24=makeQuery(id+"F9.opPattern","COPY",EDGE,{"derivedFrom":makeQuery(id+"F8.boolean.opBoolean","INTERSECT",EDGE,{"derivedFrom":[makeQuery(id+"F3.opExtrude","SWEPT_FACE",FACE,{"disambiguationData":[OSD([sQuery(id+"F2.wireOp",EDGE,"E36")])]}),makeQuery(id+"F8.opRevolve","SWEPT_FACE",FACE,{"disambiguationData":[OSD([sQuery(id+"F7.wireOp",EDGE,"E48")])]})]}),"instanceName":"-9"});
            var Q25;
            Q25=makeQuery(id+"F9.boolean.opBoolean","INTERSECT",EDGE,{"derivedFrom":[makeQuery(id+"F1.opRevolve","SWEPT_FACE",FACE,{"disambiguationData":[OSD([sQuery(id+"F0.wireOp",EDGE,"E3.trimOffspring")])]}),makeQuery(id+"F9.opPattern","COPY",FACE,{"derivedFrom":makeQuery(id+"F3.opExtrude","SWEPT_FACE",FACE,{"disambiguationData":[OSD([sQuery(id+"F2.wireOp",EDGE,"E42.filletArc")])]}),"instanceName":"-9"})]});
            var Q26;
            Q26=makeQuery(id+"F9.opPattern","COPY",EDGE,{"derivedFrom":makeQuery(id+"F8.boolean.opBoolean","INTERSECT",EDGE,{"derivedFrom":[makeQuery(id+"F5.opPattern","COPY",FACE,{"derivedFrom":makeQuery(id+"F4.opPattern","COPY",FACE,{"derivedFrom":makeQuery(id+"F3.opExtrude","SWEPT_FACE",FACE,{"disambiguationData":[OSD([sQuery(id+"F2.wireOp",EDGE,"E37")])]}),"instanceName":"1"}),"instanceName":"1"}),makeQuery(id+"F8.opRevolve","SWEPT_FACE",FACE,{"disambiguationData":[OSD([sQuery(id+"F7.wireOp",EDGE,"E48")])]})]}),"instanceName":"-10"});
            var Q27;
            Q27=makeQuery(id+"F9.opPattern","COPY",EDGE,{"derivedFrom":makeQuery(id+"F8.boolean.opBoolean","INTERSECT",EDGE,{"derivedFrom":[makeQuery(id+"F3.opExtrude","SWEPT_FACE",FACE,{"disambiguationData":[OSD([sQuery(id+"F2.wireOp",EDGE,"E39")])]}),makeQuery(id+"F8.opRevolve","SWEPT_FACE",FACE,{"disambiguationData":[OSD([sQuery(id+"F7.wireOp",EDGE,"E48")])]})]}),"instanceName":"-10"});
            var Q28;
            Q28=makeQuery(id+"F9.boolean.opBoolean","INTERSECT",EDGE,{"derivedFrom":[makeQuery(id+"F1.opRevolve","SWEPT_FACE",FACE,{"disambiguationData":[OSD([sQuery(id+"F0.wireOp",EDGE,"E3.trimOffspring")])]}),makeQuery(id+"F9.opPattern","COPY",FACE,{"derivedFrom":makeQuery(id+"F3.opExtrude","SWEPT_FACE",FACE,{"disambiguationData":[OSD([sQuery(id+"F2.wireOp",EDGE,"E39")])]}),"instanceName":"-10"})]});
            var Q29;
            Q29=makeQuery(id+"F9.boolean.opBoolean","INTERSECT",EDGE,{"derivedFrom":[makeQuery(id+"F1.opRevolve","SWEPT_FACE",FACE,{"disambiguationData":[OSD([sQuery(id+"F0.wireOp",EDGE,"E3.trimOffspring")])]}),makeQuery(id+"F9.opPattern","COPY",FACE,{"derivedFrom":makeQuery(id+"F5.opPattern","COPY",FACE,{"derivedFrom":makeQuery(id+"F4.opPattern","COPY",FACE,{"derivedFrom":makeQuery(id+"F3.opExtrude","SWEPT_FACE",FACE,{"disambiguationData":[OSD([sQuery(id+"F2.wireOp",EDGE,"E37")])]}),"instanceName":"1"}),"instanceName":"1"}),"instanceName":"-10"})]});
            var Q30;
            Q30=makeQuery(id+"F9.opPattern","COPY",EDGE,{"derivedFrom":makeQuery(id+"F8.boolean.opBoolean","INTERSECT",EDGE,{"derivedFrom":[makeQuery(id+"F5.opPattern","COPY",FACE,{"derivedFrom":makeQuery(id+"F4.opPattern","COPY",FACE,{"derivedFrom":makeQuery(id+"F3.opExtrude","SWEPT_FACE",FACE,{"disambiguationData":[OSD([sQuery(id+"F2.wireOp",EDGE,"E37")])]}),"instanceName":"1"}),"instanceName":"1"}),makeQuery(id+"F8.opRevolve","SWEPT_FACE",FACE,{"disambiguationData":[OSD([sQuery(id+"F7.wireOp",EDGE,"E48")])]})]}),"instanceName":"-11"});
            var Q31;
            Q31=makeQuery(id+"F9.boolean.opBoolean","INTERSECT",EDGE,{"derivedFrom":[makeQuery(id+"F1.opRevolve","SWEPT_FACE",FACE,{"disambiguationData":[OSD([sQuery(id+"F0.wireOp",EDGE,"E6.filletArc")])]}),makeQuery(id+"F9.opPattern","COPY",FACE,{"derivedFrom":makeQuery(id+"F5.opPattern","COPY",FACE,{"derivedFrom":makeQuery(id+"F4.opPattern","COPY",FACE,{"derivedFrom":makeQuery(id+"F3.opExtrude","SWEPT_FACE",FACE,{"disambiguationData":[OSD([sQuery(id+"F2.wireOp",EDGE,"E43.filletArc")])]}),"instanceName":"1"}),"instanceName":"1"}),"instanceName":"-11"})]});
            var Q32;
            Q32=makeQuery(id+"F9.opPattern","COPY",EDGE,{"derivedFrom":makeQuery(id+"F8.boolean.opBoolean","INTERSECT",EDGE,{"derivedFrom":[makeQuery(id+"F3.opExtrude","SWEPT_FACE",FACE,{"disambiguationData":[OSD([sQuery(id+"F2.wireOp",EDGE,"E39")])]}),makeQuery(id+"F8.opRevolve","SWEPT_FACE",FACE,{"disambiguationData":[OSD([sQuery(id+"F7.wireOp",EDGE,"E48")])]})]}),"instanceName":"-11"});
            var Q33;
            Q33=makeQuery(id+"F9.boolean.opBoolean","INTERSECT",EDGE,{"derivedFrom":[makeQuery(id+"F1.opRevolve","SWEPT_FACE",FACE,{"disambiguationData":[OSD([sQuery(id+"F0.wireOp",EDGE,"E3.trimOffspring")])]}),makeQuery(id+"F9.opPattern","COPY",FACE,{"derivedFrom":makeQuery(id+"F3.opExtrude","SWEPT_FACE",FACE,{"disambiguationData":[OSD([sQuery(id+"F2.wireOp",EDGE,"E39")])]}),"instanceName":"-11"})]});
            var Q34;
            Q34=makeQuery(id+"F9.opPattern","COPY",EDGE,{"derivedFrom":makeQuery(id+"F8.boolean.opBoolean","INTERSECT",EDGE,{"derivedFrom":[makeQuery(id+"F3.opExtrude","SWEPT_FACE",FACE,{"disambiguationData":[OSD([sQuery(id+"F2.wireOp",EDGE,"E39")])]}),makeQuery(id+"F8.opRevolve","SWEPT_FACE",FACE,{"disambiguationData":[OSD([sQuery(id+"F7.wireOp",EDGE,"E48")])]})]}),"instanceName":"-5"});
            var Q35;
            Q35=makeQuery(id+"F9.opPattern","COPY",EDGE,{"derivedFrom":makeQuery(id+"F8.boolean.opBoolean","INTERSECT",EDGE,{"derivedFrom":[makeQuery(id+"F5.opPattern","COPY",FACE,{"derivedFrom":makeQuery(id+"F4.opPattern","COPY",FACE,{"derivedFrom":makeQuery(id+"F3.opExtrude","SWEPT_FACE",FACE,{"disambiguationData":[OSD([sQuery(id+"F2.wireOp",EDGE,"E33")])]}),"instanceName":"1"}),"instanceName":"1"}),makeQuery(id+"F8.opRevolve","SWEPT_FACE",FACE,{"disambiguationData":[OSD([sQuery(id+"F7.wireOp",EDGE,"E48")])]})]}),"instanceName":"-5"});
            var Q36;
            Q36=makeQuery(id+"F9.boolean.opBoolean","INTERSECT",EDGE,{"derivedFrom":[makeQuery(id+"F1.opRevolve","SWEPT_FACE",FACE,{"disambiguationData":[OSD([sQuery(id+"F0.wireOp",EDGE,"E3.trimOffspring")])]}),makeQuery(id+"F9.opPattern","COPY",FACE,{"derivedFrom":makeQuery(id+"F5.opPattern","COPY",FACE,{"derivedFrom":makeQuery(id+"F4.opPattern","COPY",FACE,{"derivedFrom":makeQuery(id+"F3.opExtrude","SWEPT_FACE",FACE,{"disambiguationData":[OSD([sQuery(id+"F2.wireOp",EDGE,"E34")])]}),"instanceName":"1"}),"instanceName":"1"}),"instanceName":"-5"})]});
            var Q37;
            Q37=makeQuery(id+"F9.boolean.opBoolean","INTERSECT",EDGE,{"derivedFrom":[makeQuery(id+"F1.opRevolve","SWEPT_FACE",FACE,{"disambiguationData":[OSD([sQuery(id+"F0.wireOp",EDGE,"E3.trimOffspring")])]}),makeQuery(id+"F9.opPattern","COPY",FACE,{"derivedFrom":makeQuery(id+"F3.opExtrude","SWEPT_FACE",FACE,{"disambiguationData":[OSD([sQuery(id+"F2.wireOp",EDGE,"E37")])]}),"instanceName":"-5"})]});
            var Q38;
            Q38=makeQuery(id+"F9.boolean.opBoolean","INTERSECT",EDGE,{"derivedFrom":[makeQuery(id+"F1.opRevolve","SWEPT_FACE",FACE,{"disambiguationData":[OSD([sQuery(id+"F0.wireOp",EDGE,"E3.trimOffspring")])]}),makeQuery(id+"F9.opPattern","COPY",FACE,{"derivedFrom":makeQuery(id+"F5.opPattern","COPY",FACE,{"derivedFrom":makeQuery(id+"F4.opPattern","COPY",FACE,{"derivedFrom":makeQuery(id+"F3.opExtrude","SWEPT_FACE",FACE,{"disambiguationData":[OSD([sQuery(id+"F2.wireOp",EDGE,"E34")])]}),"instanceName":"1"}),"instanceName":"1"}),"instanceName":"-6"})]});
            var Q39;
            {var subQ0=makeQuery(id+"F5.opPattern","COPY",FACE,{"derivedFrom":makeQuery(id+"F4.opPattern","COPY",FACE,{"derivedFrom":makeQuery(id+"F3.opExtrude","SWEPT_FACE",FACE,{"disambiguationData":[OSD([sQuery(id+"F2.wireOp",EDGE,"E33")])]}),"instanceName":"1"}),"instanceName":"1"});Q39=makeQuery(id+"F9.boolean.opBoolean","INTERSECT",EDGE,{"disambiguationData":[OD(5.0)],"derivedFrom":[makeQuery(id+"F1.opRevolve","SWEPT_FACE",FACE,{"disambiguationData":[OSD([sQuery(id+"F0.wireOp",EDGE,"E6.filletArc")])]}),subQ0,makeQuery(id+"F9.opPattern","COPY",FACE,{"derivedFrom":subQ0,"instanceName":"-11"}),makeQuery(id+"F9.opPattern","COPY",FACE,{"derivedFrom":subQ0,"instanceName":"-10"}),makeQuery(id+"F9.opPattern","COPY",FACE,{"derivedFrom":subQ0,"instanceName":"-9"}),makeQuery(id+"F9.opPattern","COPY",FACE,{"derivedFrom":subQ0,"instanceName":"-8"}),makeQuery(id+"F9.opPattern","COPY",FACE,{"derivedFrom":subQ0,"instanceName":"-7"}),makeQuery(id+"F9.opPattern","COPY",FACE,{"derivedFrom":subQ0,"instanceName":"-6"}),makeQuery(id+"F9.opPattern","COPY",FACE,{"derivedFrom":subQ0,"instanceName":"-5"}),makeQuery(id+"F9.opPattern","COPY",FACE,{"derivedFrom":subQ0,"instanceName":"-4"}),makeQuery(id+"F9.opPattern","COPY",FACE,{"derivedFrom":subQ0,"instanceName":"-3"}),makeQuery(id+"F9.opPattern","COPY",FACE,{"derivedFrom":subQ0,"instanceName":"-2"}),makeQuery(id+"F9.opPattern","COPY",FACE,{"derivedFrom":subQ0,"instanceName":"-1"}),makeQuery(id+"F9.opPattern","COPY",FACE,{"derivedFrom":subQ0,"instanceName":"1"}),makeQuery(id+"F9.opPattern","COPY",FACE,{"derivedFrom":subQ0,"instanceName":"2"}),makeQuery(id+"F9.opPattern","COPY",FACE,{"derivedFrom":subQ0,"instanceName":"3"}),makeQuery(id+"F9.opPattern","COPY",FACE,{"derivedFrom":subQ0,"instanceName":"4"}),makeQuery(id+"F9.opPattern","COPY",FACE,{"derivedFrom":subQ0,"instanceName":"5"}),makeQuery(id+"F9.opPattern","COPY",FACE,{"derivedFrom":subQ0,"instanceName":"6"}),makeQuery(id+"F9.opPattern","COPY",FACE,{"derivedFrom":subQ0,"instanceName":"7"}),makeQuery(id+"F9.opPattern","COPY",FACE,{"derivedFrom":subQ0,"instanceName":"8"}),makeQuery(id+"F9.opPattern","COPY",FACE,{"derivedFrom":subQ0,"instanceName":"9"}),makeQuery(id+"F9.opPattern","COPY",FACE,{"derivedFrom":subQ0,"instanceName":"10"}),makeQuery(id+"F9.opPattern","COPY",FACE,{"derivedFrom":subQ0,"instanceName":"11"})]});}
            var Q40;
            Q40=makeQuery(id+"F9.opPattern","COPY",EDGE,{"derivedFrom":makeQuery(id+"F8.boolean.opBoolean","INTERSECT",EDGE,{"derivedFrom":[makeQuery(id+"F5.opPattern","COPY",FACE,{"derivedFrom":makeQuery(id+"F4.opPattern","COPY",FACE,{"derivedFrom":makeQuery(id+"F3.opExtrude","SWEPT_FACE",FACE,{"disambiguationData":[OSD([sQuery(id+"F2.wireOp",EDGE,"E33")])]}),"instanceName":"1"}),"instanceName":"1"}),makeQuery(id+"F8.opRevolve","SWEPT_FACE",FACE,{"disambiguationData":[OSD([sQuery(id+"F7.wireOp",EDGE,"E48")])]})]}),"instanceName":"-7"});
            var Q41;
            Q41=makeQuery(id+"F9.opPattern","COPY",FACE,{"derivedFrom":makeQuery(id+"F8.boolean.opBoolean","COPY",FACE,{"disambiguationData":[TD([makeQuery(id+"F5.opPattern","COPY",FACE,{"derivedFrom":makeQuery(id+"F4.opPattern","COPY",FACE,{"derivedFrom":makeQuery(id+"F3.opExtrude","SWEPT_FACE",FACE,{"disambiguationData":[OSD([sQuery(id+"F2.wireOp",EDGE,"E33")])]}),"instanceName":"1"}),"instanceName":"1"})])],"derivedFrom":makeQuery(id+"F8.opRevolve","SWEPT_FACE",FACE,{"disambiguationData":[OSD([sQuery(id+"F7.wireOp",EDGE,"E48")])]})}),"instanceName":"-6"});
            var Q42;
            Q42=makeQuery(id+"F9.opPattern","COPY",EDGE,{"derivedFrom":makeQuery(id+"F8.boolean.opBoolean","INTERSECT",EDGE,{"derivedFrom":[makeQuery(id+"F3.opExtrude","SWEPT_FACE",FACE,{"disambiguationData":[OSD([sQuery(id+"F2.wireOp",EDGE,"E39")])]}),makeQuery(id+"F8.opRevolve","SWEPT_FACE",FACE,{"disambiguationData":[OSD([sQuery(id+"F7.wireOp",EDGE,"E48")])]})]}),"instanceName":"-6"});
            var Q43;
            Q43=makeQuery(id+"F9.opPattern","COPY",EDGE,{"derivedFrom":makeQuery(id+"F8.boolean.opBoolean","INTERSECT",EDGE,{"derivedFrom":[makeQuery(id+"F3.opExtrude","SWEPT_FACE",FACE,{"disambiguationData":[OSD([sQuery(id+"F2.wireOp",EDGE,"E33")])]}),makeQuery(id+"F8.opRevolve","SWEPT_FACE",FACE,{"disambiguationData":[OSD([sQuery(id+"F7.wireOp",EDGE,"E48")])]})]}),"instanceName":"-7"});
            var Q44;
            {var subQ0=makeQuery(id+"F3.opExtrude","SWEPT_FACE",FACE,{"disambiguationData":[OSD([sQuery(id+"F2.wireOp",EDGE,"E33")])]});Q44=makeQuery(id+"F9.boolean.opBoolean","INTERSECT",EDGE,{"disambiguationData":[OD(5.0)],"derivedFrom":[makeQuery(id+"F1.opRevolve","SWEPT_FACE",FACE,{"disambiguationData":[OSD([sQuery(id+"F0.wireOp",EDGE,"E5.filletArc")])]}),subQ0,makeQuery(id+"F9.opPattern","COPY",FACE,{"derivedFrom":subQ0,"instanceName":"-11"}),makeQuery(id+"F9.opPattern","COPY",FACE,{"derivedFrom":subQ0,"instanceName":"-10"}),makeQuery(id+"F9.opPattern","COPY",FACE,{"derivedFrom":subQ0,"instanceName":"-9"}),makeQuery(id+"F9.opPattern","COPY",FACE,{"derivedFrom":subQ0,"instanceName":"-8"}),makeQuery(id+"F9.opPattern","COPY",FACE,{"derivedFrom":subQ0,"instanceName":"-7"}),makeQuery(id+"F9.opPattern","COPY",FACE,{"derivedFrom":subQ0,"instanceName":"-6"}),makeQuery(id+"F9.opPattern","COPY",FACE,{"derivedFrom":subQ0,"instanceName":"-5"}),makeQuery(id+"F9.opPattern","COPY",FACE,{"derivedFrom":subQ0,"instanceName":"-4"}),makeQuery(id+"F9.opPattern","COPY",FACE,{"derivedFrom":subQ0,"instanceName":"-3"}),makeQuery(id+"F9.opPattern","COPY",FACE,{"derivedFrom":subQ0,"instanceName":"-2"}),makeQuery(id+"F9.opPattern","COPY",FACE,{"derivedFrom":subQ0,"instanceName":"-1"}),makeQuery(id+"F9.opPattern","COPY",FACE,{"derivedFrom":subQ0,"instanceName":"1"}),makeQuery(id+"F9.opPattern","COPY",FACE,{"derivedFrom":subQ0,"instanceName":"2"}),makeQuery(id+"F9.opPattern","COPY",FACE,{"derivedFrom":subQ0,"instanceName":"3"}),makeQuery(id+"F9.opPattern","COPY",FACE,{"derivedFrom":subQ0,"instanceName":"4"}),makeQuery(id+"F9.opPattern","COPY",FACE,{"derivedFrom":subQ0,"instanceName":"5"}),makeQuery(id+"F9.opPattern","COPY",FACE,{"derivedFrom":subQ0,"instanceName":"6"}),makeQuery(id+"F9.opPattern","COPY",FACE,{"derivedFrom":subQ0,"instanceName":"7"}),makeQuery(id+"F9.opPattern","COPY",FACE,{"derivedFrom":subQ0,"instanceName":"8"}),makeQuery(id+"F9.opPattern","COPY",FACE,{"derivedFrom":subQ0,"instanceName":"9"}),makeQuery(id+"F9.opPattern","COPY",FACE,{"derivedFrom":subQ0,"instanceName":"10"}),makeQuery(id+"F9.opPattern","COPY",FACE,{"derivedFrom":subQ0,"instanceName":"11"})]});}
            var Q45;
            Q45=makeQuery(id+"F9.boolean.opBoolean","INTERSECT",EDGE,{"derivedFrom":[makeQuery(id+"F1.opRevolve","SWEPT_FACE",FACE,{"disambiguationData":[OSD([sQuery(id+"F0.wireOp",EDGE,"E5.filletArc")])]}),makeQuery(id+"F9.opPattern","COPY",FACE,{"derivedFrom":makeQuery(id+"F3.opExtrude","SWEPT_FACE",FACE,{"disambiguationData":[OSD([sQuery(id+"F2.wireOp",EDGE,"E34")])]}),"instanceName":"-6"})]});
            var Q46;
            Q46=makeQuery(id+"F9.opPattern","COPY",EDGE,{"derivedFrom":makeQuery(id+"F8.boolean.opBoolean","INTERSECT",EDGE,{"derivedFrom":[makeQuery(id+"F5.opPattern","COPY",FACE,{"derivedFrom":makeQuery(id+"F4.opPattern","COPY",FACE,{"derivedFrom":makeQuery(id+"F3.opExtrude","SWEPT_FACE",FACE,{"disambiguationData":[OSD([sQuery(id+"F2.wireOp",EDGE,"E41.filletArc")])]}),"instanceName":"1"}),"instanceName":"1"}),makeQuery(id+"F8.opRevolve","SWEPT_FACE",FACE,{"disambiguationData":[OSD([sQuery(id+"F7.wireOp",EDGE,"E48")])]})]}),"instanceName":"-3"});
            var Q47;
            Q47=makeQuery(id+"F9.boolean.opBoolean","INTERSECT",EDGE,{"derivedFrom":[makeQuery(id+"F1.opRevolve","SWEPT_FACE",FACE,{"disambiguationData":[OSD([sQuery(id+"F0.wireOp",EDGE,"E3.trimOffspring")])]}),makeQuery(id+"F9.opPattern","COPY",FACE,{"derivedFrom":makeQuery(id+"F5.opPattern","COPY",FACE,{"derivedFrom":makeQuery(id+"F4.opPattern","COPY",FACE,{"derivedFrom":makeQuery(id+"F3.opExtrude","SWEPT_FACE",FACE,{"disambiguationData":[OSD([sQuery(id+"F2.wireOp",EDGE,"E41.filletArc")])]}),"instanceName":"1"}),"instanceName":"1"}),"instanceName":"-3"})]});
            var Q48;
            Q48=makeQuery(id+"F9.boolean.opBoolean","INTERSECT",EDGE,{"derivedFrom":[makeQuery(id+"F1.opRevolve","SWEPT_FACE",FACE,{"disambiguationData":[OSD([sQuery(id+"F0.wireOp",EDGE,"E3.trimOffspring")])]}),makeQuery(id+"F9.opPattern","COPY",FACE,{"derivedFrom":makeQuery(id+"F5.opPattern","COPY",FACE,{"derivedFrom":makeQuery(id+"F4.opPattern","COPY",FACE,{"derivedFrom":makeQuery(id+"F3.opExtrude","SWEPT_FACE",FACE,{"disambiguationData":[OSD([sQuery(id+"F2.wireOp",EDGE,"E34")])]}),"instanceName":"1"}),"instanceName":"1"}),"instanceName":"-7"})]});
            var Q49;
            Q49=makeQuery(id+"F9.boolean.opBoolean","INTERSECT",EDGE,{"derivedFrom":[makeQuery(id+"F1.opRevolve","SWEPT_FACE",FACE,{"disambiguationData":[OSD([sQuery(id+"F0.wireOp",EDGE,"E3.trimOffspring")])]}),makeQuery(id+"F9.opPattern","COPY",FACE,{"derivedFrom":makeQuery(id+"F5.opPattern","COPY",FACE,{"derivedFrom":makeQuery(id+"F4.opPattern","COPY",FACE,{"derivedFrom":makeQuery(id+"F3.opExtrude","SWEPT_FACE",FACE,{"disambiguationData":[OSD([sQuery(id+"F2.wireOp",EDGE,"E36")])]}),"instanceName":"1"}),"instanceName":"1"}),"instanceName":"-7"})]});
            var Q50;
            {var subQ0=makeQuery(id+"F3.opExtrude","SWEPT_FACE",FACE,{"disambiguationData":[OSD([sQuery(id+"F2.wireOp",EDGE,"E33")])]});Q50=makeQuery(id+"F9.boolean.opBoolean","INTERSECT",EDGE,{"disambiguationData":[OD(4.0)],"derivedFrom":[makeQuery(id+"F1.opRevolve","SWEPT_FACE",FACE,{"disambiguationData":[OSD([sQuery(id+"F0.wireOp",EDGE,"E5.filletArc")])]}),subQ0,makeQuery(id+"F9.opPattern","COPY",FACE,{"derivedFrom":subQ0,"instanceName":"-11"}),makeQuery(id+"F9.opPattern","COPY",FACE,{"derivedFrom":subQ0,"instanceName":"-10"}),makeQuery(id+"F9.opPattern","COPY",FACE,{"derivedFrom":subQ0,"instanceName":"-9"}),makeQuery(id+"F9.opPattern","COPY",FACE,{"derivedFrom":subQ0,"instanceName":"-8"}),makeQuery(id+"F9.opPattern","COPY",FACE,{"derivedFrom":subQ0,"instanceName":"-7"}),makeQuery(id+"F9.opPattern","COPY",FACE,{"derivedFrom":subQ0,"instanceName":"-6"}),makeQuery(id+"F9.opPattern","COPY",FACE,{"derivedFrom":subQ0,"instanceName":"-5"}),makeQuery(id+"F9.opPattern","COPY",FACE,{"derivedFrom":subQ0,"instanceName":"-4"}),makeQuery(id+"F9.opPattern","COPY",FACE,{"derivedFrom":subQ0,"instanceName":"-3"}),makeQuery(id+"F9.opPattern","COPY",FACE,{"derivedFrom":subQ0,"instanceName":"-2"}),makeQuery(id+"F9.opPattern","COPY",FACE,{"derivedFrom":subQ0,"instanceName":"-1"}),makeQuery(id+"F9.opPattern","COPY",FACE,{"derivedFrom":subQ0,"instanceName":"1"}),makeQuery(id+"F9.opPattern","COPY",FACE,{"derivedFrom":subQ0,"instanceName":"2"}),makeQuery(id+"F9.opPattern","COPY",FACE,{"derivedFrom":subQ0,"instanceName":"3"}),makeQuery(id+"F9.opPattern","COPY",FACE,{"derivedFrom":subQ0,"instanceName":"4"}),makeQuery(id+"F9.opPattern","COPY",FACE,{"derivedFrom":subQ0,"instanceName":"5"}),makeQuery(id+"F9.opPattern","COPY",FACE,{"derivedFrom":subQ0,"instanceName":"6"}),makeQuery(id+"F9.opPattern","COPY",FACE,{"derivedFrom":subQ0,"instanceName":"7"}),makeQuery(id+"F9.opPattern","COPY",FACE,{"derivedFrom":subQ0,"instanceName":"8"}),makeQuery(id+"F9.opPattern","COPY",FACE,{"derivedFrom":subQ0,"instanceName":"9"}),makeQuery(id+"F9.opPattern","COPY",FACE,{"derivedFrom":subQ0,"instanceName":"10"}),makeQuery(id+"F9.opPattern","COPY",FACE,{"derivedFrom":subQ0,"instanceName":"11"})]});}
            var Q51;
            {var subQ0=sQuery(id+"F0.wireOp",EDGE,"E3.trimOffspring");var subQ1=sQuery(id+"F0.wireOp",EDGE,"E5.filletArc");Q51=makeQuery(id+"F9.boolean.opBoolean","SPLIT",EDGE,{"disambiguationData":[TD([makeQuery(id+"F9.opPattern","COPY",FACE,{"derivedFrom":makeQuery(id+"F3.opExtrude","SWEPT_FACE",FACE,{"disambiguationData":[OSD([sQuery(id+"F2.wireOp",EDGE,"E37")])]}),"instanceName":"-8"})])],"derivedFrom":makeQuery(id+"F1.opRevolve","SWEPT_EDGE",EDGE,{"disambiguationData":[OSD([subQ0,subQ1])]})});}
            var Q52;
            {var subQ0=sQuery(id+"F0.wireOp",EDGE,"E3.trimOffspring");var subQ1=sQuery(id+"F0.wireOp",EDGE,"E6.filletArc");Q52=makeQuery(id+"F9.boolean.opBoolean","SPLIT",EDGE,{"disambiguationData":[TD([makeQuery(id+"F5.opPattern","COPY",FACE,{"derivedFrom":makeQuery(id+"F4.opPattern","COPY",FACE,{"derivedFrom":makeQuery(id+"F3.opExtrude","SWEPT_FACE",FACE,{"disambiguationData":[OSD([sQuery(id+"F2.wireOp",EDGE,"E37")])]}),"instanceName":"1"}),"instanceName":"1"})])],"derivedFrom":makeQuery(id+"F1.opRevolve","SWEPT_EDGE",EDGE,{"disambiguationData":[OSD([subQ0,subQ1])]})});}
            var Q53;
            Q53=makeQuery(id+"F9.opPattern","COPY",EDGE,{"derivedFrom":makeQuery(id+"F5.opPattern","COPY",EDGE,{"derivedFrom":makeQuery(id+"F4.opPattern","COPY",EDGE,{"derivedFrom":makeQuery(id+"F3.opExtrude","SWEPT_EDGE",EDGE,{"disambiguationData":[OSD([sQuery(id+"F2.wireOp",EDGE,"E36"),sQuery(id+"F2.wireOp",EDGE,"E39")])]}),"instanceName":"1"}),"instanceName":"1"}),"instanceName":"-6"});
            var Q54;
            Q54=makeQuery(id+"F9.boolean.opBoolean","INTERSECT",EDGE,{"derivedFrom":[makeQuery(id+"F1.opRevolve","SWEPT_FACE",FACE,{"disambiguationData":[OSD([sQuery(id+"F0.wireOp",EDGE,"E3.trimOffspring")])]}),makeQuery(id+"F9.opPattern","COPY",FACE,{"derivedFrom":makeQuery(id+"F3.opExtrude","SWEPT_FACE",FACE,{"disambiguationData":[OSD([sQuery(id+"F2.wireOp",EDGE,"E36")])]}),"instanceName":"-7"})]});
            var Q55;
            Q55=makeQuery(id+"F8.boolean.opBoolean","INTERSECT",EDGE,{"derivedFrom":[makeQuery(id+"F5.opPattern","COPY",FACE,{"derivedFrom":makeQuery(id+"F4.opPattern","COPY",FACE,{"derivedFrom":makeQuery(id+"F3.opExtrude","SWEPT_FACE",FACE,{"disambiguationData":[OSD([sQuery(id+"F2.wireOp",EDGE,"E37")])]}),"instanceName":"1"}),"instanceName":"1"}),makeQuery(id+"F8.opRevolve","SWEPT_FACE",FACE,{"disambiguationData":[OSD([sQuery(id+"F7.wireOp",EDGE,"E48")])]})]});
            var Q56;
            Q56=makeQuery(id+"F9.opPattern","COPY",EDGE,{"derivedFrom":makeQuery(id+"F8.boolean.opBoolean","INTERSECT",EDGE,{"derivedFrom":[makeQuery(id+"F5.opPattern","COPY",FACE,{"derivedFrom":makeQuery(id+"F4.opPattern","COPY",FACE,{"derivedFrom":makeQuery(id+"F3.opExtrude","SWEPT_FACE",FACE,{"disambiguationData":[OSD([sQuery(id+"F2.wireOp",EDGE,"E37")])]}),"instanceName":"1"}),"instanceName":"1"}),makeQuery(id+"F8.opRevolve","SWEPT_FACE",FACE,{"disambiguationData":[OSD([sQuery(id+"F7.wireOp",EDGE,"E48")])]})]}),"instanceName":"-1"});
            var Q57;
            Q57=makeQuery(id+"F8.boolean.opBoolean","INTERSECT",EDGE,{"derivedFrom":[makeQuery(id+"F5.opPattern","COPY",FACE,{"derivedFrom":makeQuery(id+"F4.opPattern","COPY",FACE,{"derivedFrom":makeQuery(id+"F3.opExtrude","SWEPT_FACE",FACE,{"disambiguationData":[OSD([sQuery(id+"F2.wireOp",EDGE,"E42.filletArc")])]}),"instanceName":"1"}),"instanceName":"1"}),makeQuery(id+"F8.opRevolve","SWEPT_FACE",FACE,{"disambiguationData":[OSD([sQuery(id+"F7.wireOp",EDGE,"E48")])]})]});
            var Q58;
            Q58=makeQuery(id+"F9.opPattern","COPY",EDGE,{"derivedFrom":makeQuery(id+"F8.boolean.opBoolean","INTERSECT",EDGE,{"derivedFrom":[makeQuery(id+"F5.opPattern","COPY",FACE,{"derivedFrom":makeQuery(id+"F4.opPattern","COPY",FACE,{"derivedFrom":makeQuery(id+"F3.opExtrude","SWEPT_FACE",FACE,{"disambiguationData":[OSD([sQuery(id+"F2.wireOp",EDGE,"E40.filletArc")])]}),"instanceName":"1"}),"instanceName":"1"}),makeQuery(id+"F8.opRevolve","SWEPT_FACE",FACE,{"disambiguationData":[OSD([sQuery(id+"F7.wireOp",EDGE,"E48")])]})]}),"instanceName":"-1"});
            var Q59;
            Q59=makeQuery(id+"F9.opPattern","COPY",EDGE,{"derivedFrom":makeQuery(id+"F8.boolean.opBoolean","INTERSECT",EDGE,{"derivedFrom":[makeQuery(id+"F5.opPattern","COPY",FACE,{"derivedFrom":makeQuery(id+"F4.opPattern","COPY",FACE,{"derivedFrom":makeQuery(id+"F3.opExtrude","SWEPT_FACE",FACE,{"disambiguationData":[OSD([sQuery(id+"F2.wireOp",EDGE,"E39")])]}),"instanceName":"1"}),"instanceName":"1"}),makeQuery(id+"F8.opRevolve","SWEPT_FACE",FACE,{"disambiguationData":[OSD([sQuery(id+"F7.wireOp",EDGE,"E48")])]})]}),"instanceName":"-7"});
            var Q60;
            Q60=makeQuery(id+"F9.opPattern","COPY",EDGE,{"derivedFrom":makeQuery(id+"F8.boolean.opBoolean","INTERSECT",EDGE,{"derivedFrom":[makeQuery(id+"F3.opExtrude","SWEPT_FACE",FACE,{"disambiguationData":[OSD([sQuery(id+"F2.wireOp",EDGE,"E36")])]}),makeQuery(id+"F8.opRevolve","SWEPT_FACE",FACE,{"disambiguationData":[OSD([sQuery(id+"F7.wireOp",EDGE,"E48")])]})]}),"instanceName":"-6"});
            var Q61;
            Q61=makeQuery(id+"F9.boolean.opBoolean","INTERSECT",EDGE,{"derivedFrom":[makeQuery(id+"F1.opRevolve","SWEPT_FACE",FACE,{"disambiguationData":[OSD([sQuery(id+"F0.wireOp",EDGE,"E6.filletArc")])]}),makeQuery(id+"F9.opPattern","COPY",FACE,{"derivedFrom":makeQuery(id+"F5.opPattern","COPY",FACE,{"derivedFrom":makeQuery(id+"F4.opPattern","COPY",FACE,{"derivedFrom":makeQuery(id+"F3.opExtrude","SWEPT_FACE",FACE,{"disambiguationData":[OSD([sQuery(id+"F2.wireOp",EDGE,"E34")])]}),"instanceName":"1"}),"instanceName":"1"}),"instanceName":"-1"})]});
            var Q62;
            Q62=makeQuery(id+"F9.boolean.opBoolean","INTERSECT",EDGE,{"derivedFrom":[makeQuery(id+"F1.opRevolve","SWEPT_FACE",FACE,{"disambiguationData":[OSD([sQuery(id+"F0.wireOp",EDGE,"E5.filletArc")])]}),makeQuery(id+"F9.opPattern","COPY",FACE,{"derivedFrom":makeQuery(id+"F3.opExtrude","SWEPT_FACE",FACE,{"disambiguationData":[OSD([sQuery(id+"F2.wireOp",EDGE,"E37")])]}),"instanceName":"-8"})]});
            var Q63;
            Q63=makeQuery(id+"F9.boolean.opBoolean","INTERSECT",EDGE,{"derivedFrom":[makeQuery(id+"F1.opRevolve","SWEPT_FACE",FACE,{"disambiguationData":[OSD([sQuery(id+"F0.wireOp",EDGE,"E6.filletArc")])]}),makeQuery(id+"F5.opPattern","COPY",FACE,{"derivedFrom":makeQuery(id+"F4.opPattern","COPY",FACE,{"derivedFrom":makeQuery(id+"F3.opExtrude","SWEPT_FACE",FACE,{"disambiguationData":[OSD([sQuery(id+"F2.wireOp",EDGE,"E43.filletArc")])]}),"instanceName":"1"}),"instanceName":"1"})]});
            var Q64;
            Q64=makeQuery(id+"F9.boolean.opBoolean","INTERSECT",EDGE,{"derivedFrom":[makeQuery(id+"F1.opRevolve","SWEPT_FACE",FACE,{"disambiguationData":[OSD([sQuery(id+"F0.wireOp",EDGE,"E5.filletArc")])]}),makeQuery(id+"F9.opPattern","COPY",FACE,{"derivedFrom":makeQuery(id+"F3.opExtrude","SWEPT_FACE",FACE,{"disambiguationData":[OSD([sQuery(id+"F2.wireOp",EDGE,"E44.filletArc")])]}),"instanceName":"-8"})]});
            var Q65;
            Q65=makeQuery(id+"F8.boolean.opBoolean","INTERSECT",EDGE,{"derivedFrom":[makeQuery(id+"F5.opPattern","COPY",FACE,{"derivedFrom":makeQuery(id+"F4.opPattern","COPY",FACE,{"derivedFrom":makeQuery(id+"F3.opExtrude","SWEPT_FACE",FACE,{"disambiguationData":[OSD([sQuery(id+"F2.wireOp",EDGE,"E40.filletArc")])]}),"instanceName":"1"}),"instanceName":"1"}),makeQuery(id+"F8.opRevolve","SWEPT_FACE",FACE,{"disambiguationData":[OSD([sQuery(id+"F7.wireOp",EDGE,"E48")])]})]});
            var Q66;
            Q66=makeQuery(id+"F8.boolean.opBoolean","INTERSECT",EDGE,{"derivedFrom":[makeQuery(id+"F5.opPattern","COPY",FACE,{"derivedFrom":makeQuery(id+"F4.opPattern","COPY",FACE,{"derivedFrom":makeQuery(id+"F3.opExtrude","SWEPT_FACE",FACE,{"disambiguationData":[OSD([sQuery(id+"F2.wireOp",EDGE,"E41.filletArc")])]}),"instanceName":"1"}),"instanceName":"1"}),makeQuery(id+"F8.opRevolve","SWEPT_FACE",FACE,{"disambiguationData":[OSD([sQuery(id+"F7.wireOp",EDGE,"E48")])]})]});
            var Q67;
            Q67=makeQuery(id+"F9.opPattern","COPY",EDGE,{"derivedFrom":makeQuery(id+"F8.boolean.opBoolean","INTERSECT",EDGE,{"derivedFrom":[makeQuery(id+"F5.opPattern","COPY",FACE,{"derivedFrom":makeQuery(id+"F4.opPattern","COPY",FACE,{"derivedFrom":makeQuery(id+"F3.opExtrude","SWEPT_FACE",FACE,{"disambiguationData":[OSD([sQuery(id+"F2.wireOp",EDGE,"E43.filletArc")])]}),"instanceName":"1"}),"instanceName":"1"}),makeQuery(id+"F8.opRevolve","SWEPT_FACE",FACE,{"disambiguationData":[OSD([sQuery(id+"F7.wireOp",EDGE,"E48")])]})]}),"instanceName":"-1"});
            var Q68;
            Q68=makeQuery(id+"F9.boolean.opBoolean","INTERSECT",EDGE,{"derivedFrom":[makeQuery(id+"F1.opRevolve","SWEPT_FACE",FACE,{"disambiguationData":[OSD([sQuery(id+"F0.wireOp",EDGE,"E3.trimOffspring")])]}),makeQuery(id+"F9.opPattern","COPY",FACE,{"derivedFrom":makeQuery(id+"F3.opExtrude","SWEPT_FACE",FACE,{"disambiguationData":[OSD([sQuery(id+"F2.wireOp",EDGE,"E36")])]}),"instanceName":"-6"})]});
            var Q69;
            Q69=makeQuery(id+"F8.boolean.opBoolean","INTERSECT",EDGE,{"derivedFrom":[makeQuery(id+"F3.opExtrude","SWEPT_FACE",FACE,{"disambiguationData":[OSD([sQuery(id+"F2.wireOp",EDGE,"E34")])]}),makeQuery(id+"F8.opRevolve","SWEPT_FACE",FACE,{"disambiguationData":[OSD([sQuery(id+"F7.wireOp",EDGE,"E48")])]})]});
            var Q70;
            Q70=makeQuery(id+"F8.boolean.opBoolean","INTERSECT",EDGE,{"derivedFrom":[makeQuery(id+"F3.opExtrude","SWEPT_FACE",FACE,{"disambiguationData":[OSD([sQuery(id+"F2.wireOp",EDGE,"E37")])]}),makeQuery(id+"F8.opRevolve","SWEPT_FACE",FACE,{"disambiguationData":[OSD([sQuery(id+"F7.wireOp",EDGE,"E48")])]})]});
            var Q71;
            Q71=makeQuery(id+"F9.boolean.opBoolean","INTERSECT",EDGE,{"derivedFrom":[makeQuery(id+"F1.opRevolve","SWEPT_FACE",FACE,{"disambiguationData":[OSD([sQuery(id+"F0.wireOp",EDGE,"E3.trimOffspring")])]}),makeQuery(id+"F5.opPattern","COPY",FACE,{"derivedFrom":makeQuery(id+"F4.opPattern","COPY",FACE,{"derivedFrom":makeQuery(id+"F3.opExtrude","SWEPT_FACE",FACE,{"disambiguationData":[OSD([sQuery(id+"F2.wireOp",EDGE,"E37")])]}),"instanceName":"1"}),"instanceName":"1"})]});
            var Q72;
            Q72=makeQuery(id+"F8.boolean.opBoolean","INTERSECT",EDGE,{"derivedFrom":[makeQuery(id+"F3.opExtrude","SWEPT_FACE",FACE,{"disambiguationData":[OSD([sQuery(id+"F2.wireOp",EDGE,"E33")])]}),makeQuery(id+"F8.opRevolve","SWEPT_FACE",FACE,{"disambiguationData":[OSD([sQuery(id+"F7.wireOp",EDGE,"E48")])]})]});
            var Q73;
            Q73=makeQuery(id+"F9.opPattern","COPY",EDGE,{"derivedFrom":makeQuery(id+"F8.boolean.opBoolean","INTERSECT",EDGE,{"derivedFrom":[makeQuery(id+"F5.opPattern","COPY",FACE,{"derivedFrom":makeQuery(id+"F4.opPattern","COPY",FACE,{"derivedFrom":makeQuery(id+"F3.opExtrude","SWEPT_FACE",FACE,{"disambiguationData":[OSD([sQuery(id+"F2.wireOp",EDGE,"E36")])]}),"instanceName":"1"}),"instanceName":"1"}),makeQuery(id+"F8.opRevolve","SWEPT_FACE",FACE,{"disambiguationData":[OSD([sQuery(id+"F7.wireOp",EDGE,"E48")])]})]}),"instanceName":"-7"});
            var Q74;
            Q74=makeQuery(id+"F9.boolean.opBoolean","INTERSECT",EDGE,{"derivedFrom":[makeQuery(id+"F1.opRevolve","SWEPT_FACE",FACE,{"disambiguationData":[OSD([sQuery(id+"F0.wireOp",EDGE,"E5.filletArc")])]}),makeQuery(id+"F3.opExtrude","SWEPT_FACE",FACE,{"disambiguationData":[OSD([sQuery(id+"F2.wireOp",EDGE,"E37")])]})]});
            var Q75;
            Q75=makeQuery(id+"F9.boolean.opBoolean","INTERSECT",EDGE,{"derivedFrom":[makeQuery(id+"F1.opRevolve","SWEPT_FACE",FACE,{"disambiguationData":[OSD([sQuery(id+"F0.wireOp",EDGE,"E3.trimOffspring")])]}),makeQuery(id+"F3.opExtrude","SWEPT_FACE",FACE,{"disambiguationData":[OSD([sQuery(id+"F2.wireOp",EDGE,"E39")])]})]});
            var Q76;
            Q76=makeQuery(id+"F9.opPattern","COPY",EDGE,{"derivedFrom":makeQuery(id+"F5.opPattern","COPY",EDGE,{"derivedFrom":makeQuery(id+"F4.opPattern","COPY",EDGE,{"derivedFrom":makeQuery(id+"F3.opExtrude","SWEPT_EDGE",EDGE,{"disambiguationData":[OSD([sQuery(id+"F2.wireOp",EDGE,"E36"),sQuery(id+"F2.wireOp",EDGE,"E40.filletArc")])]}),"instanceName":"1"}),"instanceName":"1"}),"instanceName":"-7"});
            var Q77;
            Q77=makeQuery(id+"F9.boolean.opBoolean","INTERSECT",EDGE,{"derivedFrom":[makeQuery(id+"F1.opRevolve","SWEPT_FACE",FACE,{"disambiguationData":[OSD([sQuery(id+"F0.wireOp",EDGE,"E3.trimOffspring")])]}),makeQuery(id+"F9.opPattern","COPY",FACE,{"derivedFrom":makeQuery(id+"F5.opPattern","COPY",FACE,{"derivedFrom":makeQuery(id+"F4.opPattern","COPY",FACE,{"derivedFrom":makeQuery(id+"F3.opExtrude","SWEPT_FACE",FACE,{"disambiguationData":[OSD([sQuery(id+"F2.wireOp",EDGE,"E39")])]}),"instanceName":"1"}),"instanceName":"1"}),"instanceName":"-7"})]});
            var Q78;
            Q78=makeQuery(id+"F9.boolean.opBoolean","INTERSECT",EDGE,{"derivedFrom":[makeQuery(id+"F1.opRevolve","SWEPT_FACE",FACE,{"disambiguationData":[OSD([sQuery(id+"F0.wireOp",EDGE,"E6.filletArc")])]}),makeQuery(id+"F5.opPattern","COPY",FACE,{"derivedFrom":makeQuery(id+"F4.opPattern","COPY",FACE,{"derivedFrom":makeQuery(id+"F3.opExtrude","SWEPT_FACE",FACE,{"disambiguationData":[OSD([sQuery(id+"F2.wireOp",EDGE,"E37")])]}),"instanceName":"1"}),"instanceName":"1"})]});
            var Q79;
            Q79=makeQuery(id+"F8.boolean.opBoolean","INTERSECT",EDGE,{"derivedFrom":[makeQuery(id+"F3.opExtrude","SWEPT_FACE",FACE,{"disambiguationData":[OSD([sQuery(id+"F2.wireOp",EDGE,"E41.filletArc")])]}),makeQuery(id+"F8.opRevolve","SWEPT_FACE",FACE,{"disambiguationData":[OSD([sQuery(id+"F7.wireOp",EDGE,"E48")])]})]});
            var Q80;
            Q80=makeQuery(id+"F9.boolean.opBoolean","INTERSECT",EDGE,{"derivedFrom":[makeQuery(id+"F1.opRevolve","SWEPT_FACE",FACE,{"disambiguationData":[OSD([sQuery(id+"F0.wireOp",EDGE,"E5.filletArc")])]}),makeQuery(id+"F3.opExtrude","SWEPT_FACE",FACE,{"disambiguationData":[OSD([sQuery(id+"F2.wireOp",EDGE,"E44.filletArc")])]})]});
            var Q81;
            Q81=makeQuery(id+"F9.opPattern","COPY",EDGE,{"derivedFrom":makeQuery(id+"F8.boolean.opBoolean","INTERSECT",EDGE,{"derivedFrom":[makeQuery(id+"F5.opPattern","COPY",FACE,{"derivedFrom":makeQuery(id+"F4.opPattern","COPY",FACE,{"derivedFrom":makeQuery(id+"F3.opExtrude","SWEPT_FACE",FACE,{"disambiguationData":[OSD([sQuery(id+"F2.wireOp",EDGE,"E41.filletArc")])]}),"instanceName":"1"}),"instanceName":"1"}),makeQuery(id+"F8.opRevolve","SWEPT_FACE",FACE,{"disambiguationData":[OSD([sQuery(id+"F7.wireOp",EDGE,"E48")])]})]}),"instanceName":"-7"});
            var Q82;
            Q82=makeQuery(id+"F9.boolean.opBoolean","INTERSECT",EDGE,{"derivedFrom":[makeQuery(id+"F1.opRevolve","SWEPT_FACE",FACE,{"disambiguationData":[OSD([sQuery(id+"F0.wireOp",EDGE,"E3.trimOffspring")])]}),makeQuery(id+"F9.opPattern","COPY",FACE,{"derivedFrom":makeQuery(id+"F3.opExtrude","SWEPT_FACE",FACE,{"disambiguationData":[OSD([sQuery(id+"F2.wireOp",EDGE,"E34")])]}),"instanceName":"-7"})]});
            var Q83;
            Q83=makeQuery(id+"F9.boolean.opBoolean","INTERSECT",EDGE,{"derivedFrom":[makeQuery(id+"F1.opRevolve","SWEPT_FACE",FACE,{"disambiguationData":[OSD([sQuery(id+"F0.wireOp",EDGE,"E3.trimOffspring")])]}),makeQuery(id+"F9.opPattern","COPY",FACE,{"derivedFrom":makeQuery(id+"F5.opPattern","COPY",FACE,{"derivedFrom":makeQuery(id+"F4.opPattern","COPY",FACE,{"derivedFrom":makeQuery(id+"F3.opExtrude","SWEPT_FACE",FACE,{"disambiguationData":[OSD([sQuery(id+"F2.wireOp",EDGE,"E42.filletArc")])]}),"instanceName":"1"}),"instanceName":"1"}),"instanceName":"-7"})]});
            var Q84;
            Q84=makeQuery(id+"F9.boolean.opBoolean","INTERSECT",EDGE,{"derivedFrom":[makeQuery(id+"F1.opRevolve","SWEPT_FACE",FACE,{"disambiguationData":[OSD([sQuery(id+"F0.wireOp",EDGE,"E3.trimOffspring")])]}),makeQuery(id+"F5.opPattern","COPY",FACE,{"derivedFrom":makeQuery(id+"F4.opPattern","COPY",FACE,{"derivedFrom":makeQuery(id+"F3.opExtrude","SWEPT_FACE",FACE,{"disambiguationData":[OSD([sQuery(id+"F2.wireOp",EDGE,"E40.filletArc")])]}),"instanceName":"1"}),"instanceName":"1"})]});
            var Q85;
            Q85=makeQuery(id+"F9.boolean.opBoolean","INTERSECT",EDGE,{"derivedFrom":[makeQuery(id+"F1.opRevolve","SWEPT_FACE",FACE,{"disambiguationData":[OSD([sQuery(id+"F0.wireOp",EDGE,"E3.trimOffspring")])]}),makeQuery(id+"F5.opPattern","COPY",FACE,{"derivedFrom":makeQuery(id+"F4.opPattern","COPY",FACE,{"derivedFrom":makeQuery(id+"F3.opExtrude","SWEPT_FACE",FACE,{"disambiguationData":[OSD([sQuery(id+"F2.wireOp",EDGE,"E39")])]}),"instanceName":"1"}),"instanceName":"1"})]});
            var Q86;
            Q86=makeQuery(id+"F9.boolean.opBoolean","INTERSECT",EDGE,{"derivedFrom":[makeQuery(id+"F1.opRevolve","SWEPT_FACE",FACE,{"disambiguationData":[OSD([sQuery(id+"F0.wireOp",EDGE,"E3.trimOffspring")])]}),makeQuery(id+"F3.opExtrude","SWEPT_FACE",FACE,{"disambiguationData":[OSD([sQuery(id+"F2.wireOp",EDGE,"E36")])]})]});
            var Q87;
            Q87=makeQuery(id+"F9.opPattern","COPY",EDGE,{"derivedFrom":makeQuery(id+"F8.boolean.opBoolean","INTERSECT",EDGE,{"derivedFrom":[makeQuery(id+"F5.opPattern","COPY",FACE,{"derivedFrom":makeQuery(id+"F4.opPattern","COPY",FACE,{"derivedFrom":makeQuery(id+"F3.opExtrude","SWEPT_FACE",FACE,{"disambiguationData":[OSD([sQuery(id+"F2.wireOp",EDGE,"E33")])]}),"instanceName":"1"}),"instanceName":"1"}),makeQuery(id+"F8.opRevolve","SWEPT_FACE",FACE,{"disambiguationData":[OSD([sQuery(id+"F7.wireOp",EDGE,"E48")])]})]}),"instanceName":"-1"});
            var Q88;
            Q88=makeQuery(id+"F9.opPattern","COPY",EDGE,{"derivedFrom":makeQuery(id+"F8.boolean.opBoolean","INTERSECT",EDGE,{"derivedFrom":[makeQuery(id+"F5.opPattern","COPY",FACE,{"derivedFrom":makeQuery(id+"F4.opPattern","COPY",FACE,{"derivedFrom":makeQuery(id+"F3.opExtrude","SWEPT_FACE",FACE,{"disambiguationData":[OSD([sQuery(id+"F2.wireOp",EDGE,"E36")])]}),"instanceName":"1"}),"instanceName":"1"}),makeQuery(id+"F8.opRevolve","SWEPT_FACE",FACE,{"disambiguationData":[OSD([sQuery(id+"F7.wireOp",EDGE,"E48")])]})]}),"instanceName":"-1"});
            var Q89;
            Q89=makeQuery(id+"F8.boolean.opBoolean","INTERSECT",EDGE,{"derivedFrom":[makeQuery(id+"F5.opPattern","COPY",FACE,{"derivedFrom":makeQuery(id+"F4.opPattern","COPY",FACE,{"derivedFrom":makeQuery(id+"F3.opExtrude","SWEPT_FACE",FACE,{"disambiguationData":[OSD([sQuery(id+"F2.wireOp",EDGE,"E39")])]}),"instanceName":"1"}),"instanceName":"1"}),makeQuery(id+"F8.opRevolve","SWEPT_FACE",FACE,{"disambiguationData":[OSD([sQuery(id+"F7.wireOp",EDGE,"E48")])]})]});
            var Q90;
            Q90=makeQuery(id+"F9.boolean.opBoolean","INTERSECT",EDGE,{"derivedFrom":[makeQuery(id+"F1.opRevolve","SWEPT_FACE",FACE,{"disambiguationData":[OSD([sQuery(id+"F0.wireOp",EDGE,"E3.trimOffspring")])]}),makeQuery(id+"F9.opPattern","COPY",FACE,{"derivedFrom":makeQuery(id+"F5.opPattern","COPY",FACE,{"derivedFrom":makeQuery(id+"F4.opPattern","COPY",FACE,{"derivedFrom":makeQuery(id+"F3.opExtrude","SWEPT_FACE",FACE,{"disambiguationData":[OSD([sQuery(id+"F2.wireOp",EDGE,"E41.filletArc")])]}),"instanceName":"1"}),"instanceName":"1"}),"instanceName":"-7"})]});
            var Q91;
            Q91=makeQuery(id+"F8.boolean.opBoolean","INTERSECT",EDGE,{"derivedFrom":[makeQuery(id+"F3.opExtrude","SWEPT_FACE",FACE,{"disambiguationData":[OSD([sQuery(id+"F2.wireOp",EDGE,"E44.filletArc")])]}),makeQuery(id+"F8.opRevolve","SWEPT_FACE",FACE,{"disambiguationData":[OSD([sQuery(id+"F7.wireOp",EDGE,"E48")])]})]});
            var Q92;
            Q92=makeQuery(id+"F9.opPattern","COPY",EDGE,{"derivedFrom":makeQuery(id+"F8.boolean.opBoolean","INTERSECT",EDGE,{"derivedFrom":[makeQuery(id+"F5.opPattern","COPY",FACE,{"derivedFrom":makeQuery(id+"F4.opPattern","COPY",FACE,{"derivedFrom":makeQuery(id+"F3.opExtrude","SWEPT_FACE",FACE,{"disambiguationData":[OSD([sQuery(id+"F2.wireOp",EDGE,"E34")])]}),"instanceName":"1"}),"instanceName":"1"}),makeQuery(id+"F8.opRevolve","SWEPT_FACE",FACE,{"disambiguationData":[OSD([sQuery(id+"F7.wireOp",EDGE,"E48")])]})]}),"instanceName":"-1"});
            var Q93;
            Q93=makeQuery(id+"F8.boolean.opBoolean","INTERSECT",EDGE,{"derivedFrom":[makeQuery(id+"F3.opExtrude","SWEPT_FACE",FACE,{"disambiguationData":[OSD([sQuery(id+"F2.wireOp",EDGE,"E36")])]}),makeQuery(id+"F8.opRevolve","SWEPT_FACE",FACE,{"disambiguationData":[OSD([sQuery(id+"F7.wireOp",EDGE,"E48")])]})]});
            var Q94;
            Q94=makeQuery(id+"F8.boolean.opBoolean","INTERSECT",EDGE,{"derivedFrom":[makeQuery(id+"F3.opExtrude","SWEPT_FACE",FACE,{"disambiguationData":[OSD([sQuery(id+"F2.wireOp",EDGE,"E39")])]}),makeQuery(id+"F8.opRevolve","SWEPT_FACE",FACE,{"disambiguationData":[OSD([sQuery(id+"F7.wireOp",EDGE,"E48")])]})]});
            var Q95;
            Q95=makeQuery(id+"F5.opPattern","COPY",EDGE,{"derivedFrom":makeQuery(id+"F4.opPattern","COPY",EDGE,{"derivedFrom":makeQuery(id+"F3.opExtrude","SWEPT_EDGE",EDGE,{"disambiguationData":[OSD([sQuery(id+"F2.wireOp",EDGE,"E37"),sQuery(id+"F2.wireOp",EDGE,"E43.filletArc")])]}),"instanceName":"1"}),"instanceName":"1"});
            var Q96;
            Q96=makeQuery(id+"F9.boolean.opBoolean","INTERSECT",EDGE,{"derivedFrom":[makeQuery(id+"F1.opRevolve","SWEPT_FACE",FACE,{"disambiguationData":[OSD([sQuery(id+"F0.wireOp",EDGE,"E5.filletArc")])]}),makeQuery(id+"F9.opPattern","COPY",FACE,{"derivedFrom":makeQuery(id+"F3.opExtrude","SWEPT_FACE",FACE,{"disambiguationData":[OSD([sQuery(id+"F2.wireOp",EDGE,"E43.filletArc")])]}),"instanceName":"-8"})]});
            var Q97;
            Q97=makeQuery(id+"F9.opPattern","COPY",EDGE,{"derivedFrom":makeQuery(id+"F8.boolean.opBoolean","INTERSECT",EDGE,{"derivedFrom":[makeQuery(id+"F3.opExtrude","SWEPT_FACE",FACE,{"disambiguationData":[OSD([sQuery(id+"F2.wireOp",EDGE,"E36")])]}),makeQuery(id+"F8.opRevolve","SWEPT_FACE",FACE,{"disambiguationData":[OSD([sQuery(id+"F7.wireOp",EDGE,"E48")])]})]}),"instanceName":"-7"});
            var Q98;
            Q98=makeQuery(id+"F9.boolean.opBoolean","INTERSECT",EDGE,{"derivedFrom":[makeQuery(id+"F1.opRevolve","SWEPT_FACE",FACE,{"disambiguationData":[OSD([sQuery(id+"F0.wireOp",EDGE,"E3.trimOffspring")])]}),makeQuery(id+"F9.opPattern","COPY",FACE,{"derivedFrom":makeQuery(id+"F5.opPattern","COPY",FACE,{"derivedFrom":makeQuery(id+"F4.opPattern","COPY",FACE,{"derivedFrom":makeQuery(id+"F3.opExtrude","SWEPT_FACE",FACE,{"disambiguationData":[OSD([sQuery(id+"F2.wireOp",EDGE,"E42.filletArc")])]}),"instanceName":"1"}),"instanceName":"1"}),"instanceName":"-1"})]});
            var Q99;
            Q99=makeQuery(id+"F3.opExtrude","SWEPT_EDGE",EDGE,{"disambiguationData":[OSD([sQuery(id+"F2.wireOp",EDGE,"E37"),sQuery(id+"F2.wireOp",EDGE,"E40.filletArc")])]});
            var Q100;
            Q100=makeQuery(id+"F9.boolean.opBoolean","INTERSECT",EDGE,{"derivedFrom":[makeQuery(id+"F1.opRevolve","SWEPT_FACE",FACE,{"disambiguationData":[OSD([sQuery(id+"F0.wireOp",EDGE,"E3.trimOffspring")])]}),makeQuery(id+"F9.opPattern","COPY",FACE,{"derivedFrom":makeQuery(id+"F3.opExtrude","SWEPT_FACE",FACE,{"disambiguationData":[OSD([sQuery(id+"F2.wireOp",EDGE,"E41.filletArc")])]}),"instanceName":"-7"})]});
            var Q101;
            Q101=makeQuery(id+"F3.opExtrude","SWEPT_EDGE",EDGE,{"disambiguationData":[OSD([sQuery(id+"F2.wireOp",EDGE,"E36"),sQuery(id+"F2.wireOp",EDGE,"E40.filletArc")])]});
            var Q102;
            Q102=makeQuery(id+"F9.boolean.opBoolean","INTERSECT",EDGE,{"derivedFrom":[makeQuery(id+"F1.opRevolve","SWEPT_FACE",FACE,{"disambiguationData":[OSD([sQuery(id+"F0.wireOp",EDGE,"E5.filletArc")])]}),makeQuery(id+"F9.opPattern","COPY",FACE,{"derivedFrom":makeQuery(id+"F3.opExtrude","SWEPT_FACE",FACE,{"disambiguationData":[OSD([sQuery(id+"F2.wireOp",EDGE,"E43.filletArc")])]}),"instanceName":"-7"})]});
            var Q103;
            Q103=makeQuery(id+"F9.opPattern","COPY",EDGE,{"derivedFrom":makeQuery(id+"F5.opPattern","COPY",EDGE,{"derivedFrom":makeQuery(id+"F4.opPattern","COPY",EDGE,{"derivedFrom":makeQuery(id+"F3.opExtrude","SWEPT_EDGE",EDGE,{"disambiguationData":[OSD([sQuery(id+"F2.wireOp",EDGE,"E36"),sQuery(id+"F2.wireOp",EDGE,"E39")])]}),"instanceName":"1"}),"instanceName":"1"}),"instanceName":"-1"});
            var Q104;
            Q104=makeQuery(id+"F9.opPattern","COPY",EDGE,{"derivedFrom":makeQuery(id+"F8.boolean.opBoolean","INTERSECT",EDGE,{"derivedFrom":[makeQuery(id+"F3.opExtrude","SWEPT_FACE",FACE,{"disambiguationData":[OSD([sQuery(id+"F2.wireOp",EDGE,"E39")])]}),makeQuery(id+"F8.opRevolve","SWEPT_FACE",FACE,{"disambiguationData":[OSD([sQuery(id+"F7.wireOp",EDGE,"E48")])]})]}),"instanceName":"-7"});
            var Q105;
            Q105=makeQuery(id+"F9.boolean.opBoolean","INTERSECT",EDGE,{"derivedFrom":[makeQuery(id+"F1.opRevolve","SWEPT_FACE",FACE,{"disambiguationData":[OSD([sQuery(id+"F0.wireOp",EDGE,"E3.trimOffspring")])]}),makeQuery(id+"F3.opExtrude","SWEPT_FACE",FACE,{"disambiguationData":[OSD([sQuery(id+"F2.wireOp",EDGE,"E42.filletArc")])]})]});
            var Q106;
            Q106=makeQuery(id+"F9.boolean.opBoolean","INTERSECT",EDGE,{"derivedFrom":[makeQuery(id+"F1.opRevolve","SWEPT_FACE",FACE,{"disambiguationData":[OSD([sQuery(id+"F0.wireOp",EDGE,"E3.trimOffspring")])]}),makeQuery(id+"F9.opPattern","COPY",FACE,{"derivedFrom":makeQuery(id+"F5.opPattern","COPY",FACE,{"derivedFrom":makeQuery(id+"F4.opPattern","COPY",FACE,{"derivedFrom":makeQuery(id+"F3.opExtrude","SWEPT_FACE",FACE,{"disambiguationData":[OSD([sQuery(id+"F2.wireOp",EDGE,"E40.filletArc")])]}),"instanceName":"1"}),"instanceName":"1"}),"instanceName":"-1"})]});
            var Q107;
            Q107=makeQuery(id+"F9.opPattern","COPY",EDGE,{"derivedFrom":makeQuery(id+"F8.boolean.opBoolean","INTERSECT",EDGE,{"derivedFrom":[makeQuery(id+"F5.opPattern","COPY",FACE,{"derivedFrom":makeQuery(id+"F4.opPattern","COPY",FACE,{"derivedFrom":makeQuery(id+"F3.opExtrude","SWEPT_FACE",FACE,{"disambiguationData":[OSD([sQuery(id+"F2.wireOp",EDGE,"E44.filletArc")])]}),"instanceName":"1"}),"instanceName":"1"}),makeQuery(id+"F8.opRevolve","SWEPT_FACE",FACE,{"disambiguationData":[OSD([sQuery(id+"F7.wireOp",EDGE,"E48")])]})]}),"instanceName":"-1"});
            var Q108;
            Q108=makeQuery(id+"F8.boolean.opBoolean","INTERSECT",EDGE,{"derivedFrom":[makeQuery(id+"F3.opExtrude","SWEPT_FACE",FACE,{"disambiguationData":[OSD([sQuery(id+"F2.wireOp",EDGE,"E40.filletArc")])]}),makeQuery(id+"F8.opRevolve","SWEPT_FACE",FACE,{"disambiguationData":[OSD([sQuery(id+"F7.wireOp",EDGE,"E48")])]})]});
            var Q109;
            Q109=makeQuery(id+"F9.boolean.opBoolean","INTERSECT",EDGE,{"derivedFrom":[makeQuery(id+"F1.opRevolve","SWEPT_FACE",FACE,{"disambiguationData":[OSD([sQuery(id+"F0.wireOp",EDGE,"E3.trimOffspring")])]}),makeQuery(id+"F3.opExtrude","SWEPT_FACE",FACE,{"disambiguationData":[OSD([sQuery(id+"F2.wireOp",EDGE,"E34")])]})]});
            var Q110;
            Q110=makeQuery(id+"F9.boolean.opBoolean","INTERSECT",EDGE,{"derivedFrom":[makeQuery(id+"F1.opRevolve","SWEPT_FACE",FACE,{"disambiguationData":[OSD([sQuery(id+"F0.wireOp",EDGE,"E3.trimOffspring")])]}),makeQuery(id+"F9.opPattern","COPY",FACE,{"derivedFrom":makeQuery(id+"F3.opExtrude","SWEPT_FACE",FACE,{"disambiguationData":[OSD([sQuery(id+"F2.wireOp",EDGE,"E37")])]}),"instanceName":"-7"})]});
            var Q111;
            Q111=makeQuery(id+"F8.boolean.opBoolean","INTERSECT",EDGE,{"derivedFrom":[makeQuery(id+"F5.opPattern","COPY",FACE,{"derivedFrom":makeQuery(id+"F4.opPattern","COPY",FACE,{"derivedFrom":makeQuery(id+"F3.opExtrude","SWEPT_FACE",FACE,{"disambiguationData":[OSD([sQuery(id+"F2.wireOp",EDGE,"E35")])]}),"instanceName":"1"}),"instanceName":"1"}),makeQuery(id+"F8.opRevolve","SWEPT_FACE",FACE,{"disambiguationData":[OSD([sQuery(id+"F7.wireOp",EDGE,"E48")])]})]});
            var Q112;
            Q112=makeQuery(id+"F9.boolean.opBoolean","INTERSECT",EDGE,{"derivedFrom":[makeQuery(id+"F1.opRevolve","SWEPT_FACE",FACE,{"disambiguationData":[OSD([sQuery(id+"F0.wireOp",EDGE,"E3.trimOffspring")])]}),makeQuery(id+"F3.opExtrude","SWEPT_FACE",FACE,{"disambiguationData":[OSD([sQuery(id+"F2.wireOp",EDGE,"E41.filletArc")])]})]});
            var Q113;
            Q113=makeQuery(id+"F9.opPattern","COPY",EDGE,{"derivedFrom":makeQuery(id+"F8.boolean.opBoolean","INTERSECT",EDGE,{"derivedFrom":[makeQuery(id+"F5.opPattern","COPY",FACE,{"derivedFrom":makeQuery(id+"F4.opPattern","COPY",FACE,{"derivedFrom":makeQuery(id+"F3.opExtrude","SWEPT_FACE",FACE,{"disambiguationData":[OSD([sQuery(id+"F2.wireOp",EDGE,"E35")])]}),"instanceName":"1"}),"instanceName":"1"}),makeQuery(id+"F8.opRevolve","SWEPT_FACE",FACE,{"disambiguationData":[OSD([sQuery(id+"F7.wireOp",EDGE,"E48")])]})]}),"instanceName":"-7"});
            var Q114;
            Q114=makeQuery(id+"F9.boolean.opBoolean","INTERSECT",EDGE,{"derivedFrom":[makeQuery(id+"F1.opRevolve","SWEPT_FACE",FACE,{"disambiguationData":[OSD([sQuery(id+"F0.wireOp",EDGE,"E3.trimOffspring")])]}),makeQuery(id+"F9.opPattern","COPY",FACE,{"derivedFrom":makeQuery(id+"F5.opPattern","COPY",FACE,{"derivedFrom":makeQuery(id+"F4.opPattern","COPY",FACE,{"derivedFrom":makeQuery(id+"F3.opExtrude","SWEPT_FACE",FACE,{"disambiguationData":[OSD([sQuery(id+"F2.wireOp",EDGE,"E34")])]}),"instanceName":"1"}),"instanceName":"1"}),"instanceName":"-1"})]});
            var Q115;
            Q115=makeQuery(id+"F9.boolean.opBoolean","INTERSECT",EDGE,{"derivedFrom":[makeQuery(id+"F1.opRevolve","SWEPT_FACE",FACE,{"disambiguationData":[OSD([sQuery(id+"F0.wireOp",EDGE,"E3.trimOffspring")])]}),makeQuery(id+"F9.opPattern","COPY",FACE,{"derivedFrom":makeQuery(id+"F3.opExtrude","SWEPT_FACE",FACE,{"disambiguationData":[OSD([sQuery(id+"F2.wireOp",EDGE,"E40.filletArc")])]}),"instanceName":"-7"})]});
            var Q116;
            Q116=makeQuery(id+"F9.boolean.opBoolean","INTERSECT",EDGE,{"derivedFrom":[makeQuery(id+"F1.opRevolve","SWEPT_FACE",FACE,{"disambiguationData":[OSD([sQuery(id+"F0.wireOp",EDGE,"E3.trimOffspring")])]}),makeQuery(id+"F3.opExtrude","SWEPT_FACE",FACE,{"disambiguationData":[OSD([sQuery(id+"F2.wireOp",EDGE,"E37")])]})]});
            var Q117;
            Q117=makeQuery(id+"F9.opPattern","COPY",EDGE,{"derivedFrom":makeQuery(id+"F3.opExtrude","SWEPT_EDGE",EDGE,{"disambiguationData":[OSD([sQuery(id+"F2.wireOp",EDGE,"E36"),sQuery(id+"F2.wireOp",EDGE,"E40.filletArc")])]}),"instanceName":"-6"});
            var Q118;
            Q118=makeQuery(id+"F5.opPattern","COPY",EDGE,{"derivedFrom":makeQuery(id+"F4.opPattern","COPY",EDGE,{"derivedFrom":makeQuery(id+"F3.opExtrude","SWEPT_EDGE",EDGE,{"disambiguationData":[OSD([sQuery(id+"F2.wireOp",EDGE,"E36"),sQuery(id+"F2.wireOp",EDGE,"E40.filletArc")])]}),"instanceName":"1"}),"instanceName":"1"});
            var Q119;
            Q119=makeQuery(id+"F9.opPattern","COPY",EDGE,{"derivedFrom":makeQuery(id+"F8.boolean.opBoolean","INTERSECT",EDGE,{"derivedFrom":[makeQuery(id+"F3.opExtrude","SWEPT_FACE",FACE,{"disambiguationData":[OSD([sQuery(id+"F2.wireOp",EDGE,"E40.filletArc")])]}),makeQuery(id+"F8.opRevolve","SWEPT_FACE",FACE,{"disambiguationData":[OSD([sQuery(id+"F7.wireOp",EDGE,"E48")])]})]}),"instanceName":"-7"});
            var Q120;
            Q120=makeQuery(id+"F9.boolean.opBoolean","INTERSECT",EDGE,{"derivedFrom":[makeQuery(id+"F1.opRevolve","SWEPT_FACE",FACE,{"disambiguationData":[OSD([sQuery(id+"F0.wireOp",EDGE,"E6.filletArc")])]}),makeQuery(id+"F9.opPattern","COPY",FACE,{"derivedFrom":makeQuery(id+"F5.opPattern","COPY",FACE,{"derivedFrom":makeQuery(id+"F4.opPattern","COPY",FACE,{"derivedFrom":makeQuery(id+"F3.opExtrude","SWEPT_FACE",FACE,{"disambiguationData":[OSD([sQuery(id+"F2.wireOp",EDGE,"E37")])]}),"instanceName":"1"}),"instanceName":"1"}),"instanceName":"-1"})]});
            var Q121;
            Q121=makeQuery(id+"F3.opExtrude","SWEPT_EDGE",EDGE,{"disambiguationData":[OSD([sQuery(id+"F2.wireOp",EDGE,"E33"),sQuery(id+"F2.wireOp",EDGE,"E43.filletArc")])]});
            var Q122;
            Q122=makeQuery(id+"F9.opPattern","COPY",EDGE,{"derivedFrom":makeQuery(id+"F8.boolean.opBoolean","INTERSECT",EDGE,{"derivedFrom":[makeQuery(id+"F5.opPattern","COPY",FACE,{"derivedFrom":makeQuery(id+"F4.opPattern","COPY",FACE,{"derivedFrom":makeQuery(id+"F3.opExtrude","SWEPT_FACE",FACE,{"disambiguationData":[OSD([sQuery(id+"F2.wireOp",EDGE,"E41.filletArc")])]}),"instanceName":"1"}),"instanceName":"1"}),makeQuery(id+"F8.opRevolve","SWEPT_FACE",FACE,{"disambiguationData":[OSD([sQuery(id+"F7.wireOp",EDGE,"E48")])]})]}),"instanceName":"-1"});
            var Q123;
            Q123=makeQuery(id+"F9.opPattern","COPY",EDGE,{"derivedFrom":makeQuery(id+"F5.opPattern","COPY",EDGE,{"derivedFrom":makeQuery(id+"F4.opPattern","COPY",EDGE,{"derivedFrom":makeQuery(id+"F3.opExtrude","SWEPT_EDGE",EDGE,{"disambiguationData":[OSD([sQuery(id+"F2.wireOp",EDGE,"E36"),sQuery(id+"F2.wireOp",EDGE,"E40.filletArc")])]}),"instanceName":"1"}),"instanceName":"1"}),"instanceName":"-1"});
            var Q124;
            Q124=makeQuery(id+"F9.boolean.opBoolean","INTERSECT",EDGE,{"derivedFrom":[makeQuery(id+"F1.opRevolve","SWEPT_FACE",FACE,{"disambiguationData":[OSD([sQuery(id+"F0.wireOp",EDGE,"E3.trimOffspring")])]}),makeQuery(id+"F9.opPattern","COPY",FACE,{"derivedFrom":makeQuery(id+"F5.opPattern","COPY",FACE,{"derivedFrom":makeQuery(id+"F4.opPattern","COPY",FACE,{"derivedFrom":makeQuery(id+"F3.opExtrude","SWEPT_FACE",FACE,{"disambiguationData":[OSD([sQuery(id+"F2.wireOp",EDGE,"E37")])]}),"instanceName":"1"}),"instanceName":"1"}),"instanceName":"-1"})]});
            var Q125;
            Q125=makeQuery(id+"F8.boolean.opBoolean","INTERSECT",EDGE,{"derivedFrom":[makeQuery(id+"F3.opExtrude","SWEPT_FACE",FACE,{"disambiguationData":[OSD([sQuery(id+"F2.wireOp",EDGE,"E42.filletArc")])]}),makeQuery(id+"F8.opRevolve","SWEPT_FACE",FACE,{"disambiguationData":[OSD([sQuery(id+"F7.wireOp",EDGE,"E48")])]})]});
            var Q126;
            Q126=makeQuery(id+"F3.opExtrude","SWEPT_EDGE",EDGE,{"disambiguationData":[OSD([sQuery(id+"F2.wireOp",EDGE,"E33"),sQuery(id+"F2.wireOp",EDGE,"E44.filletArc")])]});
            var Q127;
            Q127=makeQuery(id+"F9.opPattern","COPY",EDGE,{"derivedFrom":makeQuery(id+"F5.opPattern","COPY",EDGE,{"derivedFrom":makeQuery(id+"F4.opPattern","COPY",EDGE,{"derivedFrom":makeQuery(id+"F3.opExtrude","SWEPT_EDGE",EDGE,{"disambiguationData":[OSD([sQuery(id+"F2.wireOp",EDGE,"E37"),sQuery(id+"F2.wireOp",EDGE,"E40.filletArc")])]}),"instanceName":"1"}),"instanceName":"1"}),"instanceName":"-1"});
            var Q128;
            Q128=makeQuery(id+"F9.opPattern","COPY",EDGE,{"derivedFrom":makeQuery(id+"F8.boolean.opBoolean","INTERSECT",EDGE,{"derivedFrom":[makeQuery(id+"F5.opPattern","COPY",FACE,{"derivedFrom":makeQuery(id+"F4.opPattern","COPY",FACE,{"derivedFrom":makeQuery(id+"F3.opExtrude","SWEPT_FACE",FACE,{"disambiguationData":[OSD([sQuery(id+"F2.wireOp",EDGE,"E42.filletArc")])]}),"instanceName":"1"}),"instanceName":"1"}),makeQuery(id+"F8.opRevolve","SWEPT_FACE",FACE,{"disambiguationData":[OSD([sQuery(id+"F7.wireOp",EDGE,"E48")])]})]}),"instanceName":"-1"});
            var Q129;
            Q129=makeQuery(id+"F9.opPattern","COPY",EDGE,{"derivedFrom":makeQuery(id+"F8.boolean.opBoolean","INTERSECT",EDGE,{"derivedFrom":[makeQuery(id+"F3.opExtrude","SWEPT_FACE",FACE,{"disambiguationData":[OSD([sQuery(id+"F2.wireOp",EDGE,"E37")])]}),makeQuery(id+"F8.opRevolve","SWEPT_FACE",FACE,{"disambiguationData":[OSD([sQuery(id+"F7.wireOp",EDGE,"E48")])]})]}),"instanceName":"-7"});
            var Q130;
            Q130=makeQuery(id+"F3.opExtrude","SWEPT_EDGE",EDGE,{"disambiguationData":[OSD([sQuery(id+"F2.wireOp",EDGE,"E36"),sQuery(id+"F2.wireOp",EDGE,"E39")])]});
            var Q131;
            Q131=makeQuery(id+"F9.opPattern","COPY",EDGE,{"derivedFrom":makeQuery(id+"F5.opPattern","COPY",EDGE,{"derivedFrom":makeQuery(id+"F4.opPattern","COPY",EDGE,{"derivedFrom":makeQuery(id+"F3.opExtrude","SWEPT_EDGE",EDGE,{"disambiguationData":[OSD([sQuery(id+"F2.wireOp",EDGE,"E37"),sQuery(id+"F2.wireOp",EDGE,"E43.filletArc")])]}),"instanceName":"1"}),"instanceName":"1"}),"instanceName":"-1"});
            var Q132;
            Q132=makeQuery(id+"F9.boolean.opBoolean","INTERSECT",EDGE,{"derivedFrom":[makeQuery(id+"F1.opRevolve","SWEPT_FACE",FACE,{"disambiguationData":[OSD([sQuery(id+"F0.wireOp",EDGE,"E3.trimOffspring")])]}),makeQuery(id+"F9.opPattern","COPY",FACE,{"derivedFrom":makeQuery(id+"F3.opExtrude","SWEPT_FACE",FACE,{"disambiguationData":[OSD([sQuery(id+"F2.wireOp",EDGE,"E41.filletArc")])]}),"instanceName":"-6"})]});
            var Q133;
            Q133=makeQuery(id+"F9.opPattern","COPY",EDGE,{"derivedFrom":makeQuery(id+"F8.boolean.opBoolean","INTERSECT",EDGE,{"derivedFrom":[makeQuery(id+"F5.opPattern","COPY",FACE,{"derivedFrom":makeQuery(id+"F4.opPattern","COPY",FACE,{"derivedFrom":makeQuery(id+"F3.opExtrude","SWEPT_FACE",FACE,{"disambiguationData":[OSD([sQuery(id+"F2.wireOp",EDGE,"E42.filletArc")])]}),"instanceName":"1"}),"instanceName":"1"}),makeQuery(id+"F8.opRevolve","SWEPT_FACE",FACE,{"disambiguationData":[OSD([sQuery(id+"F7.wireOp",EDGE,"E48")])]})]}),"instanceName":"-7"});
            var Q134;
            Q134=makeQuery(id+"F5.opPattern","COPY",EDGE,{"derivedFrom":makeQuery(id+"F4.opPattern","COPY",EDGE,{"derivedFrom":makeQuery(id+"F3.opExtrude","SWEPT_EDGE",EDGE,{"disambiguationData":[OSD([sQuery(id+"F2.wireOp",EDGE,"E34"),sQuery(id+"F2.wireOp",EDGE,"E41.filletArc")])]}),"instanceName":"1"}),"instanceName":"1"});
            var Q135;
            Q135=makeQuery(id+"F9.opPattern","COPY",EDGE,{"derivedFrom":makeQuery(id+"F5.opPattern","COPY",EDGE,{"derivedFrom":makeQuery(id+"F4.opPattern","COPY",EDGE,{"derivedFrom":makeQuery(id+"F3.opExtrude","SWEPT_EDGE",EDGE,{"disambiguationData":[OSD([sQuery(id+"F2.wireOp",EDGE,"E34"),sQuery(id+"F2.wireOp",EDGE,"E41.filletArc")])]}),"instanceName":"1"}),"instanceName":"1"}),"instanceName":"-7"});
            var Q136;
            Q136=makeQuery(id+"F9.boolean.opBoolean","INTERSECT",EDGE,{"derivedFrom":[makeQuery(id+"F1.opRevolve","SWEPT_FACE",FACE,{"disambiguationData":[OSD([sQuery(id+"F0.wireOp",EDGE,"E3.trimOffspring")])]}),makeQuery(id+"F9.opPattern","COPY",FACE,{"derivedFrom":makeQuery(id+"F3.opExtrude","SWEPT_FACE",FACE,{"disambiguationData":[OSD([sQuery(id+"F2.wireOp",EDGE,"E42.filletArc")])]}),"instanceName":"-7"})]});
            var Q137;
            Q137=makeQuery(id+"F9.boolean.opBoolean","INTERSECT",EDGE,{"derivedFrom":[makeQuery(id+"F1.opRevolve","SWEPT_FACE",FACE,{"disambiguationData":[OSD([sQuery(id+"F0.wireOp",EDGE,"E3.trimOffspring")])]}),makeQuery(id+"F3.opExtrude","SWEPT_FACE",FACE,{"disambiguationData":[OSD([sQuery(id+"F2.wireOp",EDGE,"E40.filletArc")])]})]});
            var Q138;
            Q138=makeQuery(id+"F9.boolean.opBoolean","INTERSECT",EDGE,{"derivedFrom":[makeQuery(id+"F1.opRevolve","SWEPT_FACE",FACE,{"disambiguationData":[OSD([sQuery(id+"F0.wireOp",EDGE,"E6.filletArc")])]}),makeQuery(id+"F9.opPattern","COPY",FACE,{"derivedFrom":makeQuery(id+"F5.opPattern","COPY",FACE,{"derivedFrom":makeQuery(id+"F4.opPattern","COPY",FACE,{"derivedFrom":makeQuery(id+"F3.opExtrude","SWEPT_FACE",FACE,{"disambiguationData":[OSD([sQuery(id+"F2.wireOp",EDGE,"E44.filletArc")])]}),"instanceName":"1"}),"instanceName":"1"}),"instanceName":"-1"})]});
            var Q139;
            Q139=makeQuery(id+"F9.opPattern","COPY",EDGE,{"derivedFrom":makeQuery(id+"F5.opPattern","COPY",EDGE,{"derivedFrom":makeQuery(id+"F4.opPattern","COPY",EDGE,{"derivedFrom":makeQuery(id+"F3.opExtrude","SWEPT_EDGE",EDGE,{"disambiguationData":[OSD([sQuery(id+"F2.wireOp",EDGE,"E33"),sQuery(id+"F2.wireOp",EDGE,"E43.filletArc")])]}),"instanceName":"1"}),"instanceName":"1"}),"instanceName":"-1"});
            var Q140;
            Q140=makeQuery(id+"F9.boolean.opBoolean","INTERSECT",EDGE,{"derivedFrom":[makeQuery(id+"F1.opRevolve","SWEPT_FACE",FACE,{"disambiguationData":[OSD([sQuery(id+"F0.wireOp",EDGE,"E3.trimOffspring")])]}),makeQuery(id+"F5.opPattern","COPY",FACE,{"derivedFrom":makeQuery(id+"F4.opPattern","COPY",FACE,{"derivedFrom":makeQuery(id+"F3.opExtrude","SWEPT_FACE",FACE,{"disambiguationData":[OSD([sQuery(id+"F2.wireOp",EDGE,"E41.filletArc")])]}),"instanceName":"1"}),"instanceName":"1"})]});
            var Q141;
            Q141=makeQuery(id+"F9.boolean.opBoolean","INTERSECT",EDGE,{"derivedFrom":[makeQuery(id+"F1.opRevolve","SWEPT_FACE",FACE,{"disambiguationData":[OSD([sQuery(id+"F0.wireOp",EDGE,"E3.trimOffspring")])]}),makeQuery(id+"F9.opPattern","COPY",FACE,{"derivedFrom":makeQuery(id+"F3.opExtrude","SWEPT_FACE",FACE,{"disambiguationData":[OSD([sQuery(id+"F2.wireOp",EDGE,"E39")])]}),"instanceName":"-7"})]});
            var Q142;
            Q142=makeQuery(id+"F5.opPattern","COPY",EDGE,{"derivedFrom":makeQuery(id+"F4.opPattern","COPY",EDGE,{"derivedFrom":makeQuery(id+"F3.opExtrude","SWEPT_EDGE",EDGE,{"disambiguationData":[OSD([sQuery(id+"F2.wireOp",EDGE,"E39"),sQuery(id+"F2.wireOp",EDGE,"E42.filletArc")])]}),"instanceName":"1"}),"instanceName":"1"});
            var Q143;
            Q143=makeQuery(id+"F3.opExtrude","SWEPT_EDGE",EDGE,{"disambiguationData":[OSD([sQuery(id+"F2.wireOp",EDGE,"E34"),sQuery(id+"F2.wireOp",EDGE,"E44.filletArc")])]});
            var Q144;
            Q144=makeQuery(id+"F9.boolean.opBoolean","INTERSECT",EDGE,{"derivedFrom":[makeQuery(id+"F1.opRevolve","SWEPT_FACE",FACE,{"disambiguationData":[OSD([sQuery(id+"F0.wireOp",EDGE,"E6.filletArc")])]}),makeQuery(id+"F9.opPattern","COPY",FACE,{"derivedFrom":makeQuery(id+"F5.opPattern","COPY",FACE,{"derivedFrom":makeQuery(id+"F4.opPattern","COPY",FACE,{"derivedFrom":makeQuery(id+"F3.opExtrude","SWEPT_FACE",FACE,{"disambiguationData":[OSD([sQuery(id+"F2.wireOp",EDGE,"E43.filletArc")])]}),"instanceName":"1"}),"instanceName":"1"}),"instanceName":"-1"})]});
            var Q145;
            Q145=makeQuery(id+"F9.opPattern","COPY",EDGE,{"derivedFrom":makeQuery(id+"F5.opPattern","COPY",EDGE,{"derivedFrom":makeQuery(id+"F4.opPattern","COPY",EDGE,{"derivedFrom":makeQuery(id+"F3.opExtrude","SWEPT_EDGE",EDGE,{"disambiguationData":[OSD([sQuery(id+"F2.wireOp",EDGE,"E36"),sQuery(id+"F2.wireOp",EDGE,"E39")])]}),"instanceName":"1"}),"instanceName":"1"}),"instanceName":"-7"});
            var Q146;
            Q146=makeQuery(id+"F9.opPattern","COPY",EDGE,{"derivedFrom":makeQuery(id+"F5.opPattern","COPY",EDGE,{"derivedFrom":makeQuery(id+"F4.opPattern","COPY",EDGE,{"derivedFrom":makeQuery(id+"F3.opExtrude","SWEPT_EDGE",EDGE,{"disambiguationData":[OSD([sQuery(id+"F2.wireOp",EDGE,"E39"),sQuery(id+"F2.wireOp",EDGE,"E42.filletArc")])]}),"instanceName":"1"}),"instanceName":"1"}),"instanceName":"-7"});
            var Q147;
            Q147=makeQuery(id+"F3.opExtrude","SWEPT_EDGE",EDGE,{"disambiguationData":[OSD([sQuery(id+"F2.wireOp",EDGE,"E34"),sQuery(id+"F2.wireOp",EDGE,"E41.filletArc")])]});
            var Q148;
            Q148=makeQuery(id+"F9.boolean.opBoolean","INTERSECT",EDGE,{"derivedFrom":[makeQuery(id+"F1.opRevolve","SWEPT_FACE",FACE,{"disambiguationData":[OSD([sQuery(id+"F0.wireOp",EDGE,"E5.filletArc")])]}),makeQuery(id+"F3.opExtrude","SWEPT_FACE",FACE,{"disambiguationData":[OSD([sQuery(id+"F2.wireOp",EDGE,"E34")])]})]});
            var Q149;
            Q149=makeQuery(id+"F9.boolean.opBoolean","INTERSECT",EDGE,{"derivedFrom":[makeQuery(id+"F1.opRevolve","SWEPT_FACE",FACE,{"disambiguationData":[OSD([sQuery(id+"F0.wireOp",EDGE,"E3.trimOffspring")])]}),makeQuery(id+"F9.opPattern","COPY",FACE,{"derivedFrom":makeQuery(id+"F5.opPattern","COPY",FACE,{"derivedFrom":makeQuery(id+"F4.opPattern","COPY",FACE,{"derivedFrom":makeQuery(id+"F3.opExtrude","SWEPT_FACE",FACE,{"disambiguationData":[OSD([sQuery(id+"F2.wireOp",EDGE,"E35")])]}),"instanceName":"1"}),"instanceName":"1"}),"instanceName":"-7"})]});
            var Q150;
            Q150=makeQuery(id+"F9.boolean.opBoolean","INTERSECT",EDGE,{"derivedFrom":[makeQuery(id+"F1.opRevolve","SWEPT_FACE",FACE,{"disambiguationData":[OSD([sQuery(id+"F0.wireOp",EDGE,"E3.trimOffspring")])]}),makeQuery(id+"F9.opPattern","COPY",FACE,{"derivedFrom":makeQuery(id+"F5.opPattern","COPY",FACE,{"derivedFrom":makeQuery(id+"F4.opPattern","COPY",FACE,{"derivedFrom":makeQuery(id+"F3.opExtrude","SWEPT_FACE",FACE,{"disambiguationData":[OSD([sQuery(id+"F2.wireOp",EDGE,"E36")])]}),"instanceName":"1"}),"instanceName":"1"}),"instanceName":"-1"})]});
            var Q151;
            Q151=makeQuery(id+"F5.opPattern","COPY",EDGE,{"derivedFrom":makeQuery(id+"F4.opPattern","COPY",EDGE,{"derivedFrom":makeQuery(id+"F3.opExtrude","SWEPT_EDGE",EDGE,{"disambiguationData":[OSD([sQuery(id+"F2.wireOp",EDGE,"E36"),sQuery(id+"F2.wireOp",EDGE,"E39")])]}),"instanceName":"1"}),"instanceName":"1"});
            var Q152;
            Q152=makeQuery(id+"F5.opPattern","COPY",EDGE,{"derivedFrom":makeQuery(id+"F4.opPattern","COPY",EDGE,{"derivedFrom":makeQuery(id+"F3.opExtrude","SWEPT_EDGE",EDGE,{"disambiguationData":[OSD([sQuery(id+"F2.wireOp",EDGE,"E37"),sQuery(id+"F2.wireOp",EDGE,"E40.filletArc")])]}),"instanceName":"1"}),"instanceName":"1"});
            var Q153;
            Q153=makeQuery(id+"F5.opPattern","COPY",EDGE,{"derivedFrom":makeQuery(id+"F4.opPattern","COPY",EDGE,{"derivedFrom":makeQuery(id+"F3.opExtrude","SWEPT_EDGE",EDGE,{"disambiguationData":[OSD([sQuery(id+"F2.wireOp",EDGE,"E35"),sQuery(id+"F2.wireOp",EDGE,"E41.filletArc")])]}),"instanceName":"1"}),"instanceName":"1"});
            var Q154;
            Q154=makeQuery(id+"F9.opPattern","COPY",EDGE,{"derivedFrom":makeQuery(id+"F5.opPattern","COPY",EDGE,{"derivedFrom":makeQuery(id+"F4.opPattern","COPY",EDGE,{"derivedFrom":makeQuery(id+"F3.opExtrude","SWEPT_EDGE",EDGE,{"disambiguationData":[OSD([sQuery(id+"F2.wireOp",EDGE,"E34"),sQuery(id+"F2.wireOp",EDGE,"E41.filletArc")])]}),"instanceName":"1"}),"instanceName":"1"}),"instanceName":"-1"});
            var Q155;
            Q155=makeQuery(id+"F9.opPattern","COPY",EDGE,{"derivedFrom":makeQuery(id+"F3.opExtrude","SWEPT_EDGE",EDGE,{"disambiguationData":[OSD([sQuery(id+"F2.wireOp",EDGE,"E34"),sQuery(id+"F2.wireOp",EDGE,"E41.filletArc")])]}),"instanceName":"-6"});
            var Q156;
            Q156=makeQuery(id+"F9.boolean.opBoolean","INTERSECT",EDGE,{"derivedFrom":[makeQuery(id+"F1.opRevolve","SWEPT_FACE",FACE,{"disambiguationData":[OSD([sQuery(id+"F0.wireOp",EDGE,"E3.trimOffspring")])]}),makeQuery(id+"F9.opPattern","COPY",FACE,{"derivedFrom":makeQuery(id+"F3.opExtrude","SWEPT_FACE",FACE,{"disambiguationData":[OSD([sQuery(id+"F2.wireOp",EDGE,"E39")])]}),"instanceName":"-6"})]});
            var Q157;
            Q157=makeQuery(id+"F9.boolean.opBoolean","INTERSECT",EDGE,{"derivedFrom":[makeQuery(id+"F1.opRevolve","SWEPT_FACE",FACE,{"disambiguationData":[OSD([sQuery(id+"F0.wireOp",EDGE,"E3.trimOffspring")])]}),makeQuery(id+"F3.opExtrude","SWEPT_FACE",FACE,{"disambiguationData":[OSD([sQuery(id+"F2.wireOp",EDGE,"E35")])]})]});
            var Q158;
            Q158=makeQuery(id+"F9.opPattern","COPY",EDGE,{"derivedFrom":makeQuery(id+"F3.opExtrude","SWEPT_EDGE",EDGE,{"disambiguationData":[OSD([sQuery(id+"F2.wireOp",EDGE,"E39"),sQuery(id+"F2.wireOp",EDGE,"E42.filletArc")])]}),"instanceName":"-7"});
            var Q159;
            Q159=makeQuery(id+"F9.opPattern","COPY",EDGE,{"derivedFrom":makeQuery(id+"F3.opExtrude","SWEPT_EDGE",EDGE,{"disambiguationData":[OSD([sQuery(id+"F2.wireOp",EDGE,"E36"),sQuery(id+"F2.wireOp",EDGE,"E40.filletArc")])]}),"instanceName":"-7"});
            var Q160;
            Q160=makeQuery(id+"F9.opPattern","COPY",EDGE,{"derivedFrom":makeQuery(id+"F8.boolean.opBoolean","INTERSECT",EDGE,{"derivedFrom":[makeQuery(id+"F5.opPattern","COPY",FACE,{"derivedFrom":makeQuery(id+"F4.opPattern","COPY",FACE,{"derivedFrom":makeQuery(id+"F3.opExtrude","SWEPT_FACE",FACE,{"disambiguationData":[OSD([sQuery(id+"F2.wireOp",EDGE,"E35")])]}),"instanceName":"1"}),"instanceName":"1"}),makeQuery(id+"F8.opRevolve","SWEPT_FACE",FACE,{"disambiguationData":[OSD([sQuery(id+"F7.wireOp",EDGE,"E48")])]})]}),"instanceName":"-1"});
            var Q161;
            Q161=makeQuery(id+"F9.opPattern","COPY",EDGE,{"derivedFrom":makeQuery(id+"F5.opPattern","COPY",EDGE,{"derivedFrom":makeQuery(id+"F4.opPattern","COPY",EDGE,{"derivedFrom":makeQuery(id+"F3.opExtrude","SWEPT_EDGE",EDGE,{"disambiguationData":[OSD([sQuery(id+"F2.wireOp",EDGE,"E35"),sQuery(id+"F2.wireOp",EDGE,"E41.filletArc")])]}),"instanceName":"1"}),"instanceName":"1"}),"instanceName":"-7"});
            var Q162;
            {var subQ0=makeQuery(id+"F5.opPattern","COPY",FACE,{"derivedFrom":makeQuery(id+"F4.opPattern","COPY",FACE,{"derivedFrom":makeQuery(id+"F3.opExtrude","SWEPT_FACE",FACE,{"disambiguationData":[OSD([sQuery(id+"F2.wireOp",EDGE,"E33")])]}),"instanceName":"1"}),"instanceName":"1"});Q162=makeQuery(id+"F9.boolean.opBoolean","INTERSECT",EDGE,{"disambiguationData":[OD(11.0)],"derivedFrom":[makeQuery(id+"F1.opRevolve","SWEPT_FACE",FACE,{"disambiguationData":[OSD([sQuery(id+"F0.wireOp",EDGE,"E6.filletArc")])]}),subQ0,makeQuery(id+"F9.opPattern","COPY",FACE,{"derivedFrom":subQ0,"instanceName":"-11"}),makeQuery(id+"F9.opPattern","COPY",FACE,{"derivedFrom":subQ0,"instanceName":"-10"}),makeQuery(id+"F9.opPattern","COPY",FACE,{"derivedFrom":subQ0,"instanceName":"-9"}),makeQuery(id+"F9.opPattern","COPY",FACE,{"derivedFrom":subQ0,"instanceName":"-8"}),makeQuery(id+"F9.opPattern","COPY",FACE,{"derivedFrom":subQ0,"instanceName":"-7"}),makeQuery(id+"F9.opPattern","COPY",FACE,{"derivedFrom":subQ0,"instanceName":"-6"}),makeQuery(id+"F9.opPattern","COPY",FACE,{"derivedFrom":subQ0,"instanceName":"-5"}),makeQuery(id+"F9.opPattern","COPY",FACE,{"derivedFrom":subQ0,"instanceName":"-4"}),makeQuery(id+"F9.opPattern","COPY",FACE,{"derivedFrom":subQ0,"instanceName":"-3"}),makeQuery(id+"F9.opPattern","COPY",FACE,{"derivedFrom":subQ0,"instanceName":"-2"}),makeQuery(id+"F9.opPattern","COPY",FACE,{"derivedFrom":subQ0,"instanceName":"-1"}),makeQuery(id+"F9.opPattern","COPY",FACE,{"derivedFrom":subQ0,"instanceName":"1"}),makeQuery(id+"F9.opPattern","COPY",FACE,{"derivedFrom":subQ0,"instanceName":"2"}),makeQuery(id+"F9.opPattern","COPY",FACE,{"derivedFrom":subQ0,"instanceName":"3"}),makeQuery(id+"F9.opPattern","COPY",FACE,{"derivedFrom":subQ0,"instanceName":"4"}),makeQuery(id+"F9.opPattern","COPY",FACE,{"derivedFrom":subQ0,"instanceName":"5"}),makeQuery(id+"F9.opPattern","COPY",FACE,{"derivedFrom":subQ0,"instanceName":"6"}),makeQuery(id+"F9.opPattern","COPY",FACE,{"derivedFrom":subQ0,"instanceName":"7"}),makeQuery(id+"F9.opPattern","COPY",FACE,{"derivedFrom":subQ0,"instanceName":"8"}),makeQuery(id+"F9.opPattern","COPY",FACE,{"derivedFrom":subQ0,"instanceName":"9"}),makeQuery(id+"F9.opPattern","COPY",FACE,{"derivedFrom":subQ0,"instanceName":"10"}),makeQuery(id+"F9.opPattern","COPY",FACE,{"derivedFrom":subQ0,"instanceName":"11"})]});}
            var Q163;
            Q163=makeQuery(id+"F3.opExtrude","SWEPT_EDGE",EDGE,{"disambiguationData":[OSD([sQuery(id+"F2.wireOp",EDGE,"E37"),sQuery(id+"F2.wireOp",EDGE,"E43.filletArc")])]});
            var Q164;
            Q164=makeQuery(id+"F9.boolean.opBoolean","INTERSECT",EDGE,{"derivedFrom":[makeQuery(id+"F1.opRevolve","SWEPT_FACE",FACE,{"disambiguationData":[OSD([sQuery(id+"F0.wireOp",EDGE,"E3.trimOffspring")])]}),makeQuery(id+"F5.opPattern","COPY",FACE,{"derivedFrom":makeQuery(id+"F4.opPattern","COPY",FACE,{"derivedFrom":makeQuery(id+"F3.opExtrude","SWEPT_FACE",FACE,{"disambiguationData":[OSD([sQuery(id+"F2.wireOp",EDGE,"E35")])]}),"instanceName":"1"}),"instanceName":"1"})]});
            var Q165;
            Q165=makeQuery(id+"F9.boolean.opBoolean","INTERSECT",EDGE,{"derivedFrom":[makeQuery(id+"F1.opRevolve","SWEPT_FACE",FACE,{"disambiguationData":[OSD([sQuery(id+"F0.wireOp",EDGE,"E5.filletArc")])]}),makeQuery(id+"F9.opPattern","COPY",FACE,{"derivedFrom":makeQuery(id+"F3.opExtrude","SWEPT_FACE",FACE,{"disambiguationData":[OSD([sQuery(id+"F2.wireOp",EDGE,"E37")])]}),"instanceName":"-7"})]});
            var Q166;
            Q166=makeQuery(id+"F9.boolean.opBoolean","INTERSECT",EDGE,{"derivedFrom":[makeQuery(id+"F1.opRevolve","SWEPT_FACE",FACE,{"disambiguationData":[OSD([sQuery(id+"F0.wireOp",EDGE,"E5.filletArc")])]}),makeQuery(id+"F9.opPattern","COPY",FACE,{"derivedFrom":makeQuery(id+"F3.opExtrude","SWEPT_FACE",FACE,{"disambiguationData":[OSD([sQuery(id+"F2.wireOp",EDGE,"E44.filletArc")])]}),"instanceName":"-7"})]});
            var Q167;
            Q167=makeQuery(id+"F3.opExtrude","SWEPT_EDGE",EDGE,{"disambiguationData":[OSD([sQuery(id+"F2.wireOp",EDGE,"E35"),sQuery(id+"F2.wireOp",EDGE,"E42.filletArc")])]});
            var Q168;
            Q168=makeQuery(id+"F9.boolean.opBoolean","INTERSECT",EDGE,{"derivedFrom":[makeQuery(id+"F1.opRevolve","SWEPT_FACE",FACE,{"disambiguationData":[OSD([sQuery(id+"F0.wireOp",EDGE,"E3.trimOffspring")])]}),makeQuery(id+"F9.opPattern","COPY",FACE,{"derivedFrom":makeQuery(id+"F5.opPattern","COPY",FACE,{"derivedFrom":makeQuery(id+"F4.opPattern","COPY",FACE,{"derivedFrom":makeQuery(id+"F3.opExtrude","SWEPT_FACE",FACE,{"disambiguationData":[OSD([sQuery(id+"F2.wireOp",EDGE,"E41.filletArc")])]}),"instanceName":"1"}),"instanceName":"1"}),"instanceName":"-1"})]});
            var Q169;
            Q169=makeQuery(id+"F9.opPattern","COPY",EDGE,{"derivedFrom":makeQuery(id+"F5.opPattern","COPY",EDGE,{"derivedFrom":makeQuery(id+"F4.opPattern","COPY",EDGE,{"derivedFrom":makeQuery(id+"F3.opExtrude","SWEPT_EDGE",EDGE,{"disambiguationData":[OSD([sQuery(id+"F2.wireOp",EDGE,"E33"),sQuery(id+"F2.wireOp",EDGE,"E44.filletArc")])]}),"instanceName":"1"}),"instanceName":"1"}),"instanceName":"-1"});
            var Q170;
            Q170=makeQuery(id+"F8.boolean.opBoolean","INTERSECT",EDGE,{"derivedFrom":[makeQuery(id+"F3.opExtrude","SWEPT_FACE",FACE,{"disambiguationData":[OSD([sQuery(id+"F2.wireOp",EDGE,"E43.filletArc")])]}),makeQuery(id+"F8.opRevolve","SWEPT_FACE",FACE,{"disambiguationData":[OSD([sQuery(id+"F7.wireOp",EDGE,"E48")])]})]});
            var Q171;
            Q171=makeQuery(id+"F9.opPattern","COPY",EDGE,{"derivedFrom":makeQuery(id+"F5.opPattern","COPY",EDGE,{"derivedFrom":makeQuery(id+"F4.opPattern","COPY",EDGE,{"derivedFrom":makeQuery(id+"F3.opExtrude","SWEPT_EDGE",EDGE,{"disambiguationData":[OSD([sQuery(id+"F2.wireOp",EDGE,"E34"),sQuery(id+"F2.wireOp",EDGE,"E44.filletArc")])]}),"instanceName":"1"}),"instanceName":"1"}),"instanceName":"-1"});
            var Q172;
            Q172=makeQuery(id+"F9.boolean.opBoolean","INTERSECT",EDGE,{"derivedFrom":[makeQuery(id+"F1.opRevolve","SWEPT_FACE",FACE,{"disambiguationData":[OSD([sQuery(id+"F0.wireOp",EDGE,"E3.trimOffspring")])]}),makeQuery(id+"F5.opPattern","COPY",FACE,{"derivedFrom":makeQuery(id+"F4.opPattern","COPY",FACE,{"derivedFrom":makeQuery(id+"F3.opExtrude","SWEPT_FACE",FACE,{"disambiguationData":[OSD([sQuery(id+"F2.wireOp",EDGE,"E42.filletArc")])]}),"instanceName":"1"}),"instanceName":"1"})]});
            var Q173;
            Q173=makeQuery(id+"F9.opPattern","COPY",EDGE,{"derivedFrom":makeQuery(id+"F3.opExtrude","SWEPT_EDGE",EDGE,{"disambiguationData":[OSD([sQuery(id+"F2.wireOp",EDGE,"E37"),sQuery(id+"F2.wireOp",EDGE,"E40.filletArc")])]}),"instanceName":"-7"});
            var Q174;
            Q174=makeQuery(id+"F9.boolean.opBoolean","INTERSECT",EDGE,{"derivedFrom":[makeQuery(id+"F1.opRevolve","SWEPT_FACE",FACE,{"disambiguationData":[OSD([sQuery(id+"F0.wireOp",EDGE,"E5.filletArc")])]}),makeQuery(id+"F3.opExtrude","SWEPT_FACE",FACE,{"disambiguationData":[OSD([sQuery(id+"F2.wireOp",EDGE,"E43.filletArc")])]})]});
            var Q175;
            Q175=makeQuery(id+"F9.opPattern","COPY",EDGE,{"derivedFrom":makeQuery(id+"F8.boolean.opBoolean","INTERSECT",EDGE,{"derivedFrom":[makeQuery(id+"F3.opExtrude","SWEPT_FACE",FACE,{"disambiguationData":[OSD([sQuery(id+"F2.wireOp",EDGE,"E41.filletArc")])]}),makeQuery(id+"F8.opRevolve","SWEPT_FACE",FACE,{"disambiguationData":[OSD([sQuery(id+"F7.wireOp",EDGE,"E48")])]})]}),"instanceName":"-6"});
            var Q176;
            Q176=makeQuery(id+"F9.boolean.opBoolean","INTERSECT",EDGE,{"derivedFrom":[makeQuery(id+"F1.opRevolve","SWEPT_FACE",FACE,{"disambiguationData":[OSD([sQuery(id+"F0.wireOp",EDGE,"E5.filletArc")])]}),makeQuery(id+"F9.opPattern","COPY",FACE,{"derivedFrom":makeQuery(id+"F3.opExtrude","SWEPT_FACE",FACE,{"disambiguationData":[OSD([sQuery(id+"F2.wireOp",EDGE,"E34")])]}),"instanceName":"-7"})]});
            var Q177;
            Q177=makeQuery(id+"F9.opPattern","COPY",EDGE,{"derivedFrom":makeQuery(id+"F3.opExtrude","SWEPT_EDGE",EDGE,{"disambiguationData":[OSD([sQuery(id+"F2.wireOp",EDGE,"E34"),sQuery(id+"F2.wireOp",EDGE,"E41.filletArc")])]}),"instanceName":"-7"});
            var Q178;
            Q178=makeQuery(id+"F9.opPattern","COPY",EDGE,{"derivedFrom":makeQuery(id+"F5.opPattern","COPY",EDGE,{"derivedFrom":makeQuery(id+"F4.opPattern","COPY",EDGE,{"derivedFrom":makeQuery(id+"F3.opExtrude","SWEPT_EDGE",EDGE,{"disambiguationData":[OSD([sQuery(id+"F2.wireOp",EDGE,"E39"),sQuery(id+"F2.wireOp",EDGE,"E42.filletArc")])]}),"instanceName":"1"}),"instanceName":"1"}),"instanceName":"-1"});
            var Q179;
            Q179=makeQuery(id+"F9.opPattern","COPY",EDGE,{"derivedFrom":makeQuery(id+"F8.boolean.opBoolean","INTERSECT",EDGE,{"derivedFrom":[makeQuery(id+"F3.opExtrude","SWEPT_FACE",FACE,{"disambiguationData":[OSD([sQuery(id+"F2.wireOp",EDGE,"E34")])]}),makeQuery(id+"F8.opRevolve","SWEPT_FACE",FACE,{"disambiguationData":[OSD([sQuery(id+"F7.wireOp",EDGE,"E48")])]})]}),"instanceName":"-7"});
            var Q180;
            Q180=makeQuery(id+"F3.opExtrude","SWEPT_EDGE",EDGE,{"disambiguationData":[OSD([sQuery(id+"F2.wireOp",EDGE,"E39"),sQuery(id+"F2.wireOp",EDGE,"E42.filletArc")])]});
            var Q181;
            Q181=makeQuery(id+"F9.opPattern","COPY",EDGE,{"derivedFrom":makeQuery(id+"F3.opExtrude","SWEPT_EDGE",EDGE,{"disambiguationData":[OSD([sQuery(id+"F2.wireOp",EDGE,"E36"),sQuery(id+"F2.wireOp",EDGE,"E39")])]}),"instanceName":"-7"});
            var Q182;
            Q182=makeQuery(id+"F9.opPattern","COPY",EDGE,{"derivedFrom":makeQuery(id+"F8.boolean.opBoolean","INTERSECT",EDGE,{"derivedFrom":[makeQuery(id+"F3.opExtrude","SWEPT_FACE",FACE,{"disambiguationData":[OSD([sQuery(id+"F2.wireOp",EDGE,"E42.filletArc")])]}),makeQuery(id+"F8.opRevolve","SWEPT_FACE",FACE,{"disambiguationData":[OSD([sQuery(id+"F7.wireOp",EDGE,"E48")])]})]}),"instanceName":"-7"});
            var Q183;
            Q183=makeQuery(id+"F5.opPattern","COPY",EDGE,{"derivedFrom":makeQuery(id+"F4.opPattern","COPY",EDGE,{"derivedFrom":makeQuery(id+"F3.opExtrude","SWEPT_EDGE",EDGE,{"disambiguationData":[OSD([sQuery(id+"F2.wireOp",EDGE,"E35"),sQuery(id+"F2.wireOp",EDGE,"E42.filletArc")])]}),"instanceName":"1"}),"instanceName":"1"});
            var Q184;
            Q184=makeQuery(id+"F9.boolean.opBoolean","INTERSECT",EDGE,{"derivedFrom":[makeQuery(id+"F1.opRevolve","SWEPT_FACE",FACE,{"disambiguationData":[OSD([sQuery(id+"F0.wireOp",EDGE,"E3.trimOffspring")])]}),makeQuery(id+"F9.opPattern","COPY",FACE,{"derivedFrom":makeQuery(id+"F3.opExtrude","SWEPT_FACE",FACE,{"disambiguationData":[OSD([sQuery(id+"F2.wireOp",EDGE,"E35")])]}),"instanceName":"-6"})]});
            var Q185;
            Q185=makeQuery(id+"F9.opPattern","COPY",EDGE,{"derivedFrom":makeQuery(id+"F3.opExtrude","SWEPT_EDGE",EDGE,{"disambiguationData":[OSD([sQuery(id+"F2.wireOp",EDGE,"E35"),sQuery(id+"F2.wireOp",EDGE,"E42.filletArc")])]}),"instanceName":"-7"});
            var Q186;
            Q186=makeQuery(id+"F9.opPattern","COPY",EDGE,{"derivedFrom":makeQuery(id+"F8.boolean.opBoolean","INTERSECT",EDGE,{"derivedFrom":[makeQuery(id+"F3.opExtrude","SWEPT_FACE",FACE,{"disambiguationData":[OSD([sQuery(id+"F2.wireOp",EDGE,"E42.filletArc")])]}),makeQuery(id+"F8.opRevolve","SWEPT_FACE",FACE,{"disambiguationData":[OSD([sQuery(id+"F7.wireOp",EDGE,"E48")])]})]}),"instanceName":"-6"});
            var Q187;
            Q187=makeQuery(id+"F9.opPattern","COPY",EDGE,{"derivedFrom":makeQuery(id+"F5.opPattern","COPY",EDGE,{"derivedFrom":makeQuery(id+"F4.opPattern","COPY",EDGE,{"derivedFrom":makeQuery(id+"F3.opExtrude","SWEPT_EDGE",EDGE,{"disambiguationData":[OSD([sQuery(id+"F2.wireOp",EDGE,"E35"),sQuery(id+"F2.wireOp",EDGE,"E41.filletArc")])]}),"instanceName":"1"}),"instanceName":"1"}),"instanceName":"-1"});
            var Q188;
            Q188=makeQuery(id+"F9.opPattern","COPY",EDGE,{"derivedFrom":makeQuery(id+"F3.opExtrude","SWEPT_EDGE",EDGE,{"disambiguationData":[OSD([sQuery(id+"F2.wireOp",EDGE,"E33"),sQuery(id+"F2.wireOp",EDGE,"E44.filletArc")])]}),"instanceName":"-7"});
            var Q189;
            Q189=makeQuery(id+"F9.boolean.opBoolean","INTERSECT",EDGE,{"derivedFrom":[makeQuery(id+"F1.opRevolve","SWEPT_FACE",FACE,{"disambiguationData":[OSD([sQuery(id+"F0.wireOp",EDGE,"E3.trimOffspring")])]}),makeQuery(id+"F9.opPattern","COPY",FACE,{"derivedFrom":makeQuery(id+"F3.opExtrude","SWEPT_FACE",FACE,{"disambiguationData":[OSD([sQuery(id+"F2.wireOp",EDGE,"E42.filletArc")])]}),"instanceName":"-6"})]});
            var Q190;
            Q190=makeQuery(id+"F9.boolean.opBoolean","INTERSECT",EDGE,{"derivedFrom":[makeQuery(id+"F1.opRevolve","SWEPT_FACE",FACE,{"disambiguationData":[OSD([sQuery(id+"F0.wireOp",EDGE,"E3.trimOffspring")])]}),makeQuery(id+"F9.opPattern","COPY",FACE,{"derivedFrom":makeQuery(id+"F5.opPattern","COPY",FACE,{"derivedFrom":makeQuery(id+"F4.opPattern","COPY",FACE,{"derivedFrom":makeQuery(id+"F3.opExtrude","SWEPT_FACE",FACE,{"disambiguationData":[OSD([sQuery(id+"F2.wireOp",EDGE,"E35")])]}),"instanceName":"1"}),"instanceName":"1"}),"instanceName":"-1"})]});
            var Q191;
            Q191=makeQuery(id+"F9.opPattern","COPY",EDGE,{"derivedFrom":makeQuery(id+"F3.opExtrude","SWEPT_EDGE",EDGE,{"disambiguationData":[OSD([sQuery(id+"F2.wireOp",EDGE,"E34"),sQuery(id+"F2.wireOp",EDGE,"E44.filletArc")])]}),"instanceName":"-7"});
            var Q192;
            Q192=makeQuery(id+"F9.opPattern","COPY",EDGE,{"derivedFrom":makeQuery(id+"F5.opPattern","COPY",EDGE,{"derivedFrom":makeQuery(id+"F4.opPattern","COPY",EDGE,{"derivedFrom":makeQuery(id+"F3.opExtrude","SWEPT_EDGE",EDGE,{"disambiguationData":[OSD([sQuery(id+"F2.wireOp",EDGE,"E35"),sQuery(id+"F2.wireOp",EDGE,"E42.filletArc")])]}),"instanceName":"1"}),"instanceName":"1"}),"instanceName":"-1"});
            var Q193;
            Q193=makeQuery(id+"F9.opPattern","COPY",EDGE,{"derivedFrom":makeQuery(id+"F3.opExtrude","SWEPT_EDGE",EDGE,{"disambiguationData":[OSD([sQuery(id+"F2.wireOp",EDGE,"E37"),sQuery(id+"F2.wireOp",EDGE,"E43.filletArc")])]}),"instanceName":"-7"});
            var Q194;
            Q194=makeQuery(id+"F9.opPattern","COPY",EDGE,{"derivedFrom":makeQuery(id+"F3.opExtrude","SWEPT_EDGE",EDGE,{"disambiguationData":[OSD([sQuery(id+"F2.wireOp",EDGE,"E36"),sQuery(id+"F2.wireOp",EDGE,"E39")])]}),"instanceName":"-6"});
            var Q195;
            Q195=makeQuery(id+"F9.opPattern","COPY",EDGE,{"derivedFrom":makeQuery(id+"F3.opExtrude","SWEPT_EDGE",EDGE,{"disambiguationData":[OSD([sQuery(id+"F2.wireOp",EDGE,"E33"),sQuery(id+"F2.wireOp",EDGE,"E43.filletArc")])]}),"instanceName":"-7"});
            var Q196;
            Q196=makeQuery(id+"F9.opPattern","COPY",EDGE,{"derivedFrom":makeQuery(id+"F5.opPattern","COPY",EDGE,{"derivedFrom":makeQuery(id+"F4.opPattern","COPY",EDGE,{"derivedFrom":makeQuery(id+"F3.opExtrude","SWEPT_EDGE",EDGE,{"disambiguationData":[OSD([sQuery(id+"F2.wireOp",EDGE,"E35"),sQuery(id+"F2.wireOp",EDGE,"E42.filletArc")])]}),"instanceName":"1"}),"instanceName":"1"}),"instanceName":"-7"});
            var Q197;
            Q197=makeQuery(id+"F9.opPattern","COPY",EDGE,{"derivedFrom":makeQuery(id+"F8.boolean.opBoolean","INTERSECT",EDGE,{"derivedFrom":[makeQuery(id+"F3.opExtrude","SWEPT_FACE",FACE,{"disambiguationData":[OSD([sQuery(id+"F2.wireOp",EDGE,"E41.filletArc")])]}),makeQuery(id+"F8.opRevolve","SWEPT_FACE",FACE,{"disambiguationData":[OSD([sQuery(id+"F7.wireOp",EDGE,"E48")])]})]}),"instanceName":"-7"});
            var Q198;
            Q198=makeQuery(id+"F3.opExtrude","SWEPT_EDGE",EDGE,{"disambiguationData":[OSD([sQuery(id+"F2.wireOp",EDGE,"E35"),sQuery(id+"F2.wireOp",EDGE,"E41.filletArc")])]});
            var Q199;
            Q199=makeQuery(id+"F9.opPattern","COPY",EDGE,{"derivedFrom":makeQuery(id+"F8.boolean.opBoolean","INTERSECT",EDGE,{"derivedFrom":[makeQuery(id+"F3.opExtrude","SWEPT_FACE",FACE,{"disambiguationData":[OSD([sQuery(id+"F2.wireOp",EDGE,"E43.filletArc")])]}),makeQuery(id+"F8.opRevolve","SWEPT_FACE",FACE,{"disambiguationData":[OSD([sQuery(id+"F7.wireOp",EDGE,"E48")])]})]}),"instanceName":"-7"});
            var Q200;
            Q200=makeQuery(id+"F9.opPattern","COPY",EDGE,{"derivedFrom":makeQuery(id+"F8.boolean.opBoolean","INTERSECT",EDGE,{"derivedFrom":[makeQuery(id+"F3.opExtrude","SWEPT_FACE",FACE,{"disambiguationData":[OSD([sQuery(id+"F2.wireOp",EDGE,"E35")])]}),makeQuery(id+"F8.opRevolve","SWEPT_FACE",FACE,{"disambiguationData":[OSD([sQuery(id+"F7.wireOp",EDGE,"E48")])]})]}),"instanceName":"-7"});
            var Q201;
            Q201=makeQuery(id+"F9.opPattern","COPY",EDGE,{"derivedFrom":makeQuery(id+"F3.opExtrude","SWEPT_EDGE",EDGE,{"disambiguationData":[OSD([sQuery(id+"F2.wireOp",EDGE,"E35"),sQuery(id+"F2.wireOp",EDGE,"E41.filletArc")])]}),"instanceName":"-6"});
            var Q202;
            Q202=makeQuery(id+"F9.opPattern","COPY",EDGE,{"derivedFrom":makeQuery(id+"F3.opExtrude","SWEPT_EDGE",EDGE,{"disambiguationData":[OSD([sQuery(id+"F2.wireOp",EDGE,"E39"),sQuery(id+"F2.wireOp",EDGE,"E42.filletArc")])]}),"instanceName":"-6"});
            var Q203;
            Q203=makeQuery(id+"F9.boolean.opBoolean","INTERSECT",EDGE,{"derivedFrom":[makeQuery(id+"F1.opRevolve","SWEPT_FACE",FACE,{"disambiguationData":[OSD([sQuery(id+"F0.wireOp",EDGE,"E3.trimOffspring")])]}),makeQuery(id+"F9.opPattern","COPY",FACE,{"derivedFrom":makeQuery(id+"F3.opExtrude","SWEPT_FACE",FACE,{"disambiguationData":[OSD([sQuery(id+"F2.wireOp",EDGE,"E35")])]}),"instanceName":"-7"})]});
            var Q204;
            Q204=makeQuery(id+"F9.opPattern","COPY",EDGE,{"derivedFrom":makeQuery(id+"F8.boolean.opBoolean","INTERSECT",EDGE,{"derivedFrom":[makeQuery(id+"F3.opExtrude","SWEPT_FACE",FACE,{"disambiguationData":[OSD([sQuery(id+"F2.wireOp",EDGE,"E35")])]}),makeQuery(id+"F8.opRevolve","SWEPT_FACE",FACE,{"disambiguationData":[OSD([sQuery(id+"F7.wireOp",EDGE,"E48")])]})]}),"instanceName":"-6"});
            var Q205;
            Q205=makeQuery(id+"F9.opPattern","COPY",EDGE,{"derivedFrom":makeQuery(id+"F8.boolean.opBoolean","INTERSECT",EDGE,{"derivedFrom":[makeQuery(id+"F3.opExtrude","SWEPT_FACE",FACE,{"disambiguationData":[OSD([sQuery(id+"F2.wireOp",EDGE,"E44.filletArc")])]}),makeQuery(id+"F8.opRevolve","SWEPT_FACE",FACE,{"disambiguationData":[OSD([sQuery(id+"F7.wireOp",EDGE,"E48")])]})]}),"instanceName":"-7"});
            var Q206;
            Q206=makeQuery(id+"F9.opPattern","COPY",EDGE,{"derivedFrom":makeQuery(id+"F3.opExtrude","SWEPT_EDGE",EDGE,{"disambiguationData":[OSD([sQuery(id+"F2.wireOp",EDGE,"E35"),sQuery(id+"F2.wireOp",EDGE,"E41.filletArc")])]}),"instanceName":"-7"});
            var Q207;
            Q207=makeQuery(id+"F9.opPattern","COPY",EDGE,{"derivedFrom":makeQuery(id+"F3.opExtrude","SWEPT_EDGE",EDGE,{"disambiguationData":[OSD([sQuery(id+"F2.wireOp",EDGE,"E35"),sQuery(id+"F2.wireOp",EDGE,"E42.filletArc")])]}),"instanceName":"-6"});
            fillet(context, id + "F10", {"entities" : qUnion([Q0, Q1, Q2, Q3, Q4, Q5, Q6, Q7, Q8, Q9, Q10, Q11, Q12, Q13, Q14, Q15, Q16, Q17, Q18, Q19, Q20, Q21, Q22, Q23, Q24, Q25, Q26, Q27, Q28, Q29, Q30, Q31, Q32, Q33, Q34, Q35, Q36, Q37, Q38, Q39, Q40, Q41, Q42, Q43, Q44, Q45, Q46, Q47, Q48, Q49, Q50, Q51, Q52, Q53, Q54, Q55, Q56, Q57, Q58, Q59, Q60, Q61, Q62, Q63, Q64, Q65, Q66, Q67, Q68, Q69, Q70, Q71, Q72, Q73, Q74, Q75, Q76, Q77, Q78, Q79, Q80, Q81, Q82, Q83, Q84, Q85, Q86, Q87, Q88, Q89, Q90, Q91, Q92, Q93, Q94, Q95, Q96, Q97, Q98, Q99, Q100, Q101, Q102, Q103, Q104, Q105, Q106, Q107, Q108, Q109, Q110, Q111, Q112, Q113, Q114, Q115, Q116, Q117, Q118, Q119, Q120, Q121, Q122, Q123, Q124, Q125, Q126, Q127, Q128, Q129, Q130, Q131, Q132, Q133, Q134, Q135, Q136, Q137, Q138, Q139, Q140, Q141, Q142, Q143, Q144, Q145, Q146, Q147, Q148, Q149, Q150, Q151, Q152, Q153, Q154, Q155, Q156, Q157, Q158, Q159, Q160, Q161, Q162, Q163, Q164, Q165, Q166, Q167, Q168, Q169, Q170, Q171, Q172, Q173, Q174, Q175, Q176, Q177, Q178, Q179, Q180, Q181, Q182, Q183, Q184, Q185, Q186, Q187, Q188, Q189, Q190, Q191, Q192, Q193, Q194, Q195, Q196, Q197, Q198, Q199, Q200, Q201, Q202, Q203, Q204, Q205, Q206, Q207]), "radius" : 12.7 * mm, "tangentPropagation" : true, "allowEdgeOverflow" : false});
        }
        {
            var Q0;
            Q0=qCreatedBy(makeId("Front.planeOp"),FACE);
            var sketch = newSketch(context, id + "F11", { "sketchPlane" : qUnion([Q0])});
            skLineSegment(sketch, "E54", {"start": v(-431.3, 0) * mm, "end": v(380.66, 0) * mm, "construction": true});
            skLineSegment(sketch, "E55", {"start": v(380.66, 0) * mm, "end": v(266.7, 0) * mm});
            skLineSegment(sketch, "E56", {"start": v(266.7, 0) * mm, "end": v(266.7, 190.5) * mm});
            skLineSegment(sketch, "E57", {"start": v(266.7, 190.5) * mm, "end": v(-266.7, 190.5) * mm});
            skLineSegment(sketch, "E58", {"start": v(-266.7, 190.5) * mm, "end": v(-266.7, 0) * mm});
            skLineSegment(sketch, "E59", {"start": v(-127, 190.5) * mm, "end": v(-127, 411.35) * mm});
            skLineSegment(sketch, "E60", {"start": v(-127, 460.4) * mm, "end": v(127, 460.4) * mm, "construction": true});
            skLineSegment(sketch, "E61", {"start": v(127, 411.35) * mm, "end": v(127, 190.5) * mm});
            skArc(sketch, "E62", {"start": v(77.54, 462.13) * mm, "mid": v(0, 463.16) * mm, "end": v(-77.54, 462.13) * mm});
            skLineSegment(sketch, "E63", {"start": v(0, -2470.54) * mm, "end": v(0, 751.33) * mm, "construction": true});
            skPoint(sketch, "E64.visualSharp", {"position": v(-127, 460.4) * mm});
            skArc(sketch, "E64.filletArc", {"start": v(-77.54, 462.13) * mm, "mid": v(-112.6, 446.8) * mm, "end": v(-127, 411.35) * mm});
            skPoint(sketch, "E65.visualSharp", {"position": v(127, 460.4) * mm});
            skArc(sketch, "E65.filletArc", {"start": v(127, 411.35) * mm, "mid": v(112.6, 446.8) * mm, "end": v(77.54, 462.13) * mm});
            skLineSegment(sketch, "E66", {"start": v(-266.7, 0) * mm, "end": v(266.7, 0) * mm});
            skSolve(sketch);
        }
        {
            var Q0;
            Q0 = qSketchRegion(id + "F11", true);
            var Q1;
            Q1=sQuery(id+"F11.wireOp",EDGE,"E54");
            revolve(context, id + "F12", {"operationType" : NewBodyOperationType.REMOVE, "surfaceOperationType" : NewSurfaceOperationType.NEW, "entities" : qUnion([Q0]), "axis" : qUnion([Q1]), "revolveType" : RevolveType.FULL, "oppositeDirection" : true});
        }
        {
            var Q0;
            Q0=makeQuery(id+"F1.opRevolve","SWEPT_EDGE",EDGE,{"disambiguationData":[OSD([sQuery(id+"F0.wireOp",EDGE,"E8"),sQuery(id+"F0.wireOp",EDGE,"E10"),sQuery(id+"F0.wireOp",EDGE,"E11")])]});
            var Q1;
            Q1=makeQuery(id+"F12.boolean.opBoolean","COPY",EDGE,{"derivedFrom":makeQuery(id+"F12.opRevolve","SWEPT_EDGE",EDGE,{"disambiguationData":[OSD([sQuery(id+"F11.wireOp",EDGE,"E57"),sQuery(id+"F11.wireOp",EDGE,"E59")])]})});
            var Q2;
            Q2=makeQuery(id+"F12.boolean.opBoolean","COPY",EDGE,{"derivedFrom":makeQuery(id+"F12.opRevolve","SWEPT_EDGE",EDGE,{"disambiguationData":[OSD([sQuery(id+"F11.wireOp",EDGE,"E57"),sQuery(id+"F11.wireOp",EDGE,"E61")])]})});
            var Q3;
            Q3=makeQuery(id+"F1.opRevolve","SWEPT_EDGE",EDGE,{"disambiguationData":[OSD([sQuery(id+"F0.wireOp",EDGE,"E9"),sQuery(id+"F0.wireOp",EDGE,"E10"),sQuery(id+"F0.wireOp",EDGE,"E12")])]});
            fillet(context, id + "F13", {"entities" : qUnion([Q0, Q1, Q2, Q3]), "radius" : 22.22 * mm, "tangentPropagation" : true, "allowEdgeOverflow" : false});
        }
    });
